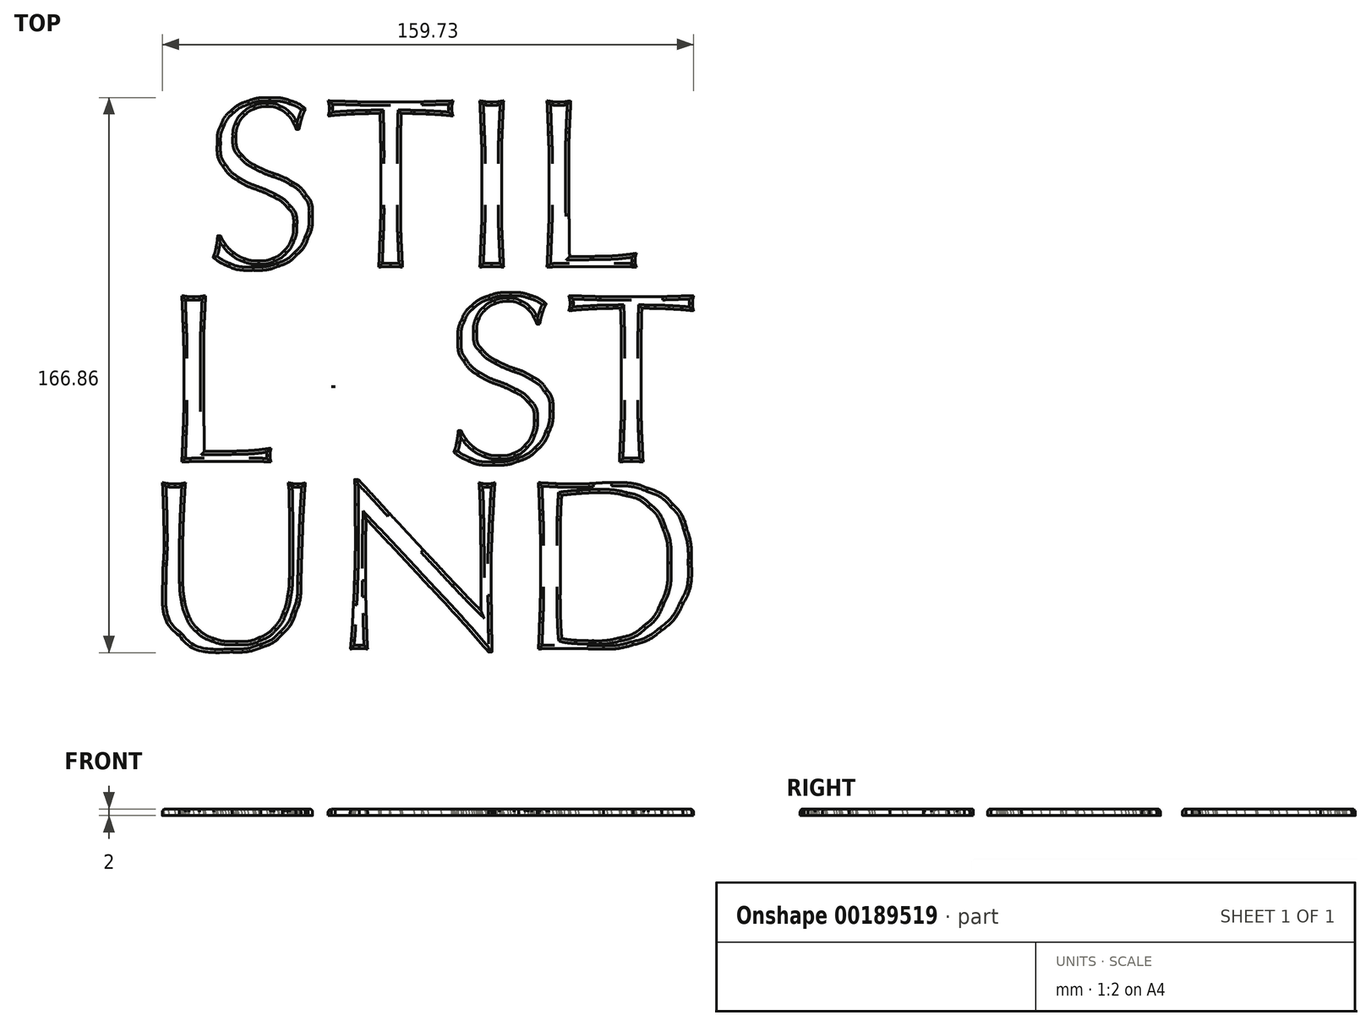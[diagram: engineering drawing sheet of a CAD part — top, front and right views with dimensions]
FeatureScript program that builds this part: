
annotation { "Feature Type Name" : "Feature", "Feature Type Description" : "" }
export const myFeature = defineFeature(function(context is Context, id is Id, definition is map)
    precondition{}
    {
        {
            var Q0;
            Q0=qCreatedBy(makeId("Top.planeOp"),FACE);
            var sketch = newSketch(context, id + "F0", { "sketchPlane" : qUnion([Q0])});
            skFitSpline(sketch, "E0", {"points": [v(-63.23, 41.86) * mm, v(-63.38, 40.46) * mm, v(-63.55, 39.3) * mm, v(-63.74, 38.37) * mm]});
            skFitSpline(sketch, "E1", {"points": [v(-63.74, 38.37) * mm, v(-63.9, 37.5) * mm, v(-64.18, 36.5) * mm, v(-64.62, 35.39) * mm]});
            skFitSpline(sketch, "E2", {"points": [v(-64.62, 35.39) * mm, v(-63.36, 34.37) * mm, v(-61.8, 33.44) * mm, v(-59.96, 32.62) * mm]});
            skFitSpline(sketch, "E3", {"points": [v(-59.96, 32.62) * mm, v(-58.07, 31.84) * mm, v(-55.62, 31.46) * mm, v(-52.6, 31.46) * mm]});
            skFitSpline(sketch, "E4", {"points": [v(-52.6, 31.46) * mm, v(-49.8, 31.46) * mm, v(-47.3, 31.84) * mm, v(-45.11, 32.62) * mm]});
            skFitSpline(sketch, "E5", {"points": [v(-45.11, 32.62) * mm, v(-42.88, 33.44) * mm, v(-41.01, 34.58) * mm, v(-39.5, 36.04) * mm]});
            skFitSpline(sketch, "E6", {"points": [v(-39.5, 36.04) * mm, v(-37.96, 37.54) * mm, v(-36.8, 39.3) * mm, v(-36.02, 41.28) * mm]});
            skFitSpline(sketch, "E7", {"points": [v(-36.02, 41.28) * mm, v(-35.2, 43.27) * mm, v(-34.78, 45.38) * mm, v(-34.78, 47.61) * mm]});
            skFitSpline(sketch, "E8", {"points": [v(-34.78, 47.61) * mm, v(-34.78, 50.28) * mm, v(-35.36, 52.42) * mm, v(-36.52, 54.02) * mm]});
            skFitSpline(sketch, "E9", {"points": [v(-36.52, 54.02) * mm, v(-37.64, 55.62) * mm, v(-39.05, 56.93) * mm, v(-40.75, 57.95) * mm]});
            skFitSpline(sketch, "E10", {"points": [v(-40.75, 57.95) * mm, v(-42.44, 58.97) * mm, v(-44.29, 59.82) * mm, v(-46.28, 60.5) * mm]});
            skFitSpline(sketch, "E11", {"points": [v(-46.28, 60.5) * mm, v(-48.22, 61.22) * mm, v(-50.04, 62.02) * mm, v(-51.74, 62.9) * mm]});
            skFitSpline(sketch, "E12", {"points": [v(-51.74, 62.9) * mm, v(-53.43, 63.82) * mm, v(-54.87, 64.93) * mm, v(-56.03, 66.24) * mm]});
            skFitSpline(sketch, "E13", {"points": [v(-56.03, 66.24) * mm, v(-57.15, 67.55) * mm, v(-57.7, 69.35) * mm, v(-57.7, 71.63) * mm]});
            skFitSpline(sketch, "E14", {"points": [v(-57.7, 71.63) * mm, v(-57.7, 72.94) * mm, v(-57.49, 74.15) * mm, v(-57.05, 75.27) * mm]});
            skFitSpline(sketch, "E15", {"points": [v(-57.05, 75.27) * mm, v(-56.56, 76.38) * mm, v(-55.9, 77.33) * mm, v(-55.08, 78.1) * mm]});
            skFitSpline(sketch, "E16", {"points": [v(-55.08, 78.1) * mm, v(-54.21, 78.93) * mm, v(-53.22, 79.56) * mm, v(-52.1, 80) * mm]});
            skFitSpline(sketch, "E17", {"points": [v(-52.1, 80) * mm, v(-50.94, 80.44) * mm, v(-49.67, 80.65) * mm, v(-48.32, 80.65) * mm]});
            skFitSpline(sketch, "E18", {"points": [v(-48.32, 80.65) * mm, v(-46.96, 80.65) * mm, v(-45.8, 80.41) * mm, v(-44.82, 79.93) * mm]});
            skFitSpline(sketch, "E19", {"points": [v(-44.82, 79.93) * mm, v(-43.85, 79.5) * mm, v(-43.03, 78.93) * mm, v(-42.35, 78.25) * mm]});
            skFitSpline(sketch, "E20", {"points": [v(-42.35, 78.25) * mm, v(-41.62, 77.57) * mm, v(-41.06, 76.82) * mm, v(-40.67, 76) * mm]});
            skFitSpline(sketch, "E21", {"points": [v(-40.67, 76) * mm, v(-40.24, 75.22) * mm, v(-39.9, 74.5) * mm, v(-39.65, 73.81) * mm]});
            skLineSegment(sketch, "E22", {"start": v(-62.36, 41.86) * mm, "end": v(-63.23, 41.86) * mm});
            skLineSegment(sketch, "E23", {"start": v(-63.23, 41.86) * mm, "end": v(-62.36, 41.86) * mm});
            skFitSpline(sketch, "E24", {"points": [v(-38.78, 73.81) * mm, v(-38.49, 75.22) * mm, v(-38.2, 76.38) * mm, v(-37.9, 77.3) * mm]});
            skFitSpline(sketch, "E25", {"points": [v(-37.9, 77.3) * mm, v(-37.62, 78.23) * mm, v(-37.25, 79.1) * mm, v(-36.82, 79.93) * mm]});
            skFitSpline(sketch, "E26", {"points": [v(-36.82, 79.93) * mm, v(-38.27, 81.1) * mm, v(-39.85, 81.94) * mm, v(-41.55, 82.47) * mm]});
            skFitSpline(sketch, "E27", {"points": [v(-41.55, 82.47) * mm, v(-43.24, 83.06) * mm, v(-45.26, 83.35) * mm, v(-47.59, 83.35) * mm]});
            skFitSpline(sketch, "E28", {"points": [v(-47.59, 83.35) * mm, v(-50.01, 83.35) * mm, v(-52.2, 83) * mm, v(-54.14, 82.33) * mm]});
            skFitSpline(sketch, "E29", {"points": [v(-54.14, 82.33) * mm, v(-56.08, 81.65) * mm, v(-57.75, 80.7) * mm, v(-59.16, 79.5) * mm]});
            skFitSpline(sketch, "E30", {"points": [v(-59.16, 79.5) * mm, v(-60.52, 78.28) * mm, v(-61.56, 76.82) * mm, v(-62.29, 75.12) * mm]});
            skFitSpline(sketch, "E31", {"points": [v(-62.29, 75.12) * mm, v(-63.02, 73.47) * mm, v(-63.38, 71.63) * mm, v(-63.38, 69.6) * mm]});
            skFitSpline(sketch, "E32", {"points": [v(-63.38, 69.6) * mm, v(-63.38, 66.73) * mm, v(-62.82, 64.45) * mm, v(-61.7, 62.75) * mm]});
            skFitSpline(sketch, "E33", {"points": [v(-61.7, 62.75) * mm, v(-60.54, 61.05) * mm, v(-59.11, 59.65) * mm, v(-57.41, 58.53) * mm]});
            skFitSpline(sketch, "E34", {"points": [v(-57.41, 58.53) * mm, v(-55.71, 57.46) * mm, v(-53.9, 56.56) * mm, v(-51.95, 55.84) * mm]});
            skFitSpline(sketch, "E35", {"points": [v(-51.95, 55.84) * mm, v(-49.96, 55.1) * mm, v(-48.12, 54.3) * mm, v(-46.42, 53.43) * mm]});
            skFitSpline(sketch, "E36", {"points": [v(-46.42, 53.43) * mm, v(-44.72, 52.56) * mm, v(-43.32, 51.47) * mm, v(-42.2, 50.16) * mm]});
            skFitSpline(sketch, "E37", {"points": [v(-42.2, 50.16) * mm, v(-41.04, 48.85) * mm, v(-40.45, 47.08) * mm, v(-40.45, 44.85) * mm]});
            skFitSpline(sketch, "E38", {"points": [v(-40.45, 44.85) * mm, v(-40.45, 43.4) * mm, v(-40.7, 42) * mm, v(-41.18, 40.7) * mm]});
            skFitSpline(sketch, "E39", {"points": [v(-41.18, 40.7) * mm, v(-41.67, 39.44) * mm, v(-42.37, 38.32) * mm, v(-43.3, 37.35) * mm]});
            skFitSpline(sketch, "E40", {"points": [v(-43.3, 37.35) * mm, v(-44.17, 36.43) * mm, v(-45.26, 35.68) * mm, v(-46.57, 35.1) * mm]});
            skFitSpline(sketch, "E41", {"points": [v(-46.57, 35.1) * mm, v(-47.83, 34.56) * mm, v(-49.26, 34.3) * mm, v(-50.86, 34.3) * mm]});
            skFitSpline(sketch, "E42", {"points": [v(-50.86, 34.3) * mm, v(-52.41, 34.3) * mm, v(-53.82, 34.51) * mm, v(-55.08, 34.95) * mm]});
            skFitSpline(sketch, "E43", {"points": [v(-55.08, 34.95) * mm, v(-56.35, 35.43) * mm, v(-57.46, 36.04) * mm, v(-58.43, 36.77) * mm]});
            skFitSpline(sketch, "E44", {"points": [v(-58.43, 36.77) * mm, v(-59.35, 37.5) * mm, v(-60.15, 38.3) * mm, v(-60.83, 39.17) * mm]});
            skFitSpline(sketch, "E45", {"points": [v(-60.83, 39.17) * mm, v(-61.46, 40.1) * mm, v(-61.97, 40.99) * mm, v(-62.36, 41.86) * mm]});
            skLineSegment(sketch, "E46", {"start": v(-39.65, 73.81) * mm, "end": v(-38.78, 73.81) * mm});
            skLineSegment(sketch, "E47", {"start": v(-38.78, 73.81) * mm, "end": v(-39.65, 73.81) * mm});
            skFitSpline(sketch, "E48", {"points": [v(-14.25, 51.03) * mm, v(-14.25, 47.83) * mm, v(-14.33, 44.68) * mm, v(-14.47, 41.57) * mm]});
            skFitSpline(sketch, "E49", {"points": [v(-14.47, 41.57) * mm, v(-14.57, 38.47) * mm, v(-14.7, 35.4) * mm, v(-14.84, 32.4) * mm]});
            skFitSpline(sketch, "E50", {"points": [v(-14.84, 32.4) * mm, v(-13.72, 32.5) * mm, v(-12.53, 32.55) * mm, v(-11.27, 32.55) * mm]});
            skFitSpline(sketch, "E51", {"points": [v(-11.27, 32.55) * mm, v(-10, 32.55) * mm, v(-8.82, 32.5) * mm, v(-7.7, 32.4) * mm]});
            skFitSpline(sketch, "E52", {"points": [v(-7.7, 32.4) * mm, v(-7.85, 35.4) * mm, v(-8, 38.47) * mm, v(-8.14, 41.57) * mm]});
            skFitSpline(sketch, "E53", {"points": [v(-8.14, 41.57) * mm, v(-8.24, 44.68) * mm, v(-8.29, 47.83) * mm, v(-8.29, 51.03) * mm]});
            skLineSegment(sketch, "E54", {"start": v(-14.25, 63.55) * mm, "end": v(-14.25, 51.03) * mm});
            skLineSegment(sketch, "E55", {"start": v(-14.25, 51.03) * mm, "end": v(-14.25, 63.55) * mm});
            skFitSpline(sketch, "E56", {"points": [v(-8.29, 63.55) * mm, v(-8.29, 68.6) * mm, v(-8.21, 73.62) * mm, v(-8.07, 78.62) * mm]});
            skFitSpline(sketch, "E57", {"points": [v(-8.07, 78.62) * mm, v(-6.8, 78.62) * mm, v(-5.5, 78.6) * mm, v(-4.14, 78.54) * mm]});
            skFitSpline(sketch, "E58", {"points": [v(-4.14, 78.54) * mm, v(-2.73, 78.54) * mm, v(-1.35, 78.5) * mm, v(0.01, 78.4) * mm]});
            skFitSpline(sketch, "E59", {"points": [v(0.01, 78.4) * mm, v(1.42, 78.35) * mm, v(2.75, 78.28) * mm, v(4.01, 78.18) * mm]});
            skFitSpline(sketch, "E60", {"points": [v(4.01, 78.18) * mm, v(5.32, 78.08) * mm, v(6.49, 77.96) * mm, v(7.5, 77.82) * mm]});
            skFitSpline(sketch, "E61", {"points": [v(7.5, 77.82) * mm, v(7.26, 78.69) * mm, v(7.14, 79.44) * mm, v(7.14, 80.07) * mm]});
            skFitSpline(sketch, "E62", {"points": [v(7.14, 80.07) * mm, v(7.14, 80.65) * mm, v(7.26, 81.43) * mm, v(7.5, 82.4) * mm]});
            skFitSpline(sketch, "E63", {"points": [v(7.5, 82.4) * mm, v(4.3, 82.3) * mm, v(1.18, 82.2) * mm, v(-1.88, 82.11) * mm]});
            skFitSpline(sketch, "E64", {"points": [v(-1.88, 82.11) * mm, v(-4.94, 82.06) * mm, v(-8.07, 82.04) * mm, v(-11.27, 82.04) * mm]});
            skFitSpline(sketch, "E65", {"points": [v(-11.27, 82.04) * mm, v(-14.47, 82.04) * mm, v(-17.6, 82.06) * mm, v(-20.66, 82.11) * mm]});
            skFitSpline(sketch, "E66", {"points": [v(-20.66, 82.11) * mm, v(-23.72, 82.2) * mm, v(-26.84, 82.3) * mm, v(-30.05, 82.4) * mm]});
            skFitSpline(sketch, "E67", {"points": [v(-30.05, 82.4) * mm, v(-29.8, 81.43) * mm, v(-29.68, 80.68) * mm, v(-29.68, 80.15) * mm]});
            skFitSpline(sketch, "E68", {"points": [v(-29.68, 80.15) * mm, v(-29.68, 79.47) * mm, v(-29.8, 78.69) * mm, v(-30.05, 77.82) * mm]});
            skFitSpline(sketch, "E69", {"points": [v(-30.05, 77.82) * mm, v(-29.03, 77.96) * mm, v(-27.89, 78.08) * mm, v(-26.63, 78.18) * mm]});
            skFitSpline(sketch, "E70", {"points": [v(-26.63, 78.18) * mm, v(-25.32, 78.28) * mm, v(-23.98, 78.35) * mm, v(-22.62, 78.4) * mm]});
            skFitSpline(sketch, "E71", {"points": [v(-22.62, 78.4) * mm, v(-21.22, 78.5) * mm, v(-19.83, 78.54) * mm, v(-18.48, 78.54) * mm]});
            skFitSpline(sketch, "E72", {"points": [v(-18.48, 78.54) * mm, v(-17.07, 78.6) * mm, v(-15.73, 78.62) * mm, v(-14.47, 78.62) * mm]});
            skFitSpline(sketch, "E73", {"points": [v(-14.47, 78.62) * mm, v(-14.33, 73.62) * mm, v(-14.25, 68.6) * mm, v(-14.25, 63.55) * mm]});
            skLineSegment(sketch, "E74", {"start": v(-8.29, 51.03) * mm, "end": v(-8.29, 63.55) * mm});
            skLineSegment(sketch, "E75", {"start": v(-8.29, 63.55) * mm, "end": v(-8.29, 51.03) * mm});
            skFitSpline(sketch, "E76", {"points": [v(16.14, 51.03) * mm, v(16.14, 47.83) * mm, v(16.07, 44.68) * mm, v(15.92, 41.57) * mm]});
            skFitSpline(sketch, "E77", {"points": [v(15.92, 41.57) * mm, v(15.83, 38.47) * mm, v(15.7, 35.4) * mm, v(15.56, 32.4) * mm]});
            skFitSpline(sketch, "E78", {"points": [v(15.56, 32.4) * mm, v(16.68, 32.5) * mm, v(17.86, 32.55) * mm, v(19.13, 32.55) * mm]});
            skFitSpline(sketch, "E79", {"points": [v(19.13, 32.55) * mm, v(20.39, 32.55) * mm, v(21.58, 32.5) * mm, v(22.7, 32.4) * mm]});
            skFitSpline(sketch, "E80", {"points": [v(22.7, 32.4) * mm, v(22.55, 35.4) * mm, v(22.4, 38.47) * mm, v(22.26, 41.57) * mm]});
            skFitSpline(sketch, "E81", {"points": [v(22.26, 41.57) * mm, v(22.16, 44.68) * mm, v(22.11, 47.83) * mm, v(22.11, 51.03) * mm]});
            skLineSegment(sketch, "E82", {"start": v(16.14, 63.55) * mm, "end": v(16.14, 51.03) * mm});
            skLineSegment(sketch, "E83", {"start": v(16.14, 51.03) * mm, "end": v(16.14, 63.55) * mm});
            skFitSpline(sketch, "E84", {"points": [v(22.11, 63.55) * mm, v(22.11, 66.75) * mm, v(22.16, 69.88) * mm, v(22.26, 72.94) * mm]});
            skFitSpline(sketch, "E85", {"points": [v(22.26, 72.94) * mm, v(22.4, 76.05) * mm, v(22.55, 79.2) * mm, v(22.7, 82.4) * mm]});
            skFitSpline(sketch, "E86", {"points": [v(22.7, 82.4) * mm, v(22.06, 82.3) * mm, v(21.46, 82.2) * mm, v(20.87, 82.11) * mm]});
            skFitSpline(sketch, "E87", {"points": [v(20.87, 82.11) * mm, v(20.3, 82.06) * mm, v(19.7, 82.04) * mm, v(19.13, 82.04) * mm]});
            skFitSpline(sketch, "E88", {"points": [v(19.13, 82.04) * mm, v(18.54, 82.04) * mm, v(17.96, 82.06) * mm, v(17.38, 82.11) * mm]});
            skFitSpline(sketch, "E89", {"points": [v(17.38, 82.11) * mm, v(16.8, 82.2) * mm, v(16.2, 82.3) * mm, v(15.56, 82.4) * mm]});
            skFitSpline(sketch, "E90", {"points": [v(15.56, 82.4) * mm, v(15.7, 79.2) * mm, v(15.83, 76.05) * mm, v(15.92, 72.94) * mm]});
            skFitSpline(sketch, "E91", {"points": [v(15.92, 72.94) * mm, v(16.07, 69.88) * mm, v(16.14, 66.75) * mm, v(16.14, 63.55) * mm]});
            skLineSegment(sketch, "E92", {"start": v(22.11, 51.03) * mm, "end": v(22.11, 63.55) * mm});
            skLineSegment(sketch, "E93", {"start": v(22.11, 63.55) * mm, "end": v(22.11, 51.03) * mm});
            skFitSpline(sketch, "E94", {"points": [v(36.33, 51.03) * mm, v(36.33, 47.83) * mm, v(36.25, 44.68) * mm, v(36.1, 41.57) * mm]});
            skFitSpline(sketch, "E95", {"points": [v(36.1, 41.57) * mm, v(36.01, 38.47) * mm, v(35.9, 35.4) * mm, v(35.74, 32.4) * mm]});
            skFitSpline(sketch, "E96", {"points": [v(35.74, 32.4) * mm, v(38.07, 32.5) * mm, v(40.3, 32.55) * mm, v(42.44, 32.55) * mm]});
            skFitSpline(sketch, "E97", {"points": [v(42.44, 32.55) * mm, v(44.62, 32.55) * mm, v(46.88, 32.55) * mm, v(49.2, 32.55) * mm]});
            skFitSpline(sketch, "E98", {"points": [v(49.2, 32.55) * mm, v(51.44, 32.55) * mm, v(53.67, 32.55) * mm, v(55.9, 32.55) * mm]});
            skFitSpline(sketch, "E99", {"points": [v(55.9, 32.55) * mm, v(58.14, 32.55) * mm, v(60.37, 32.5) * mm, v(62.6, 32.4) * mm]});
            skFitSpline(sketch, "E100", {"points": [v(62.6, 32.4) * mm, v(62.36, 33.18) * mm, v(62.24, 33.83) * mm, v(62.24, 34.37) * mm]});
            skFitSpline(sketch, "E101", {"points": [v(62.24, 34.37) * mm, v(62.24, 34.95) * mm, v(62.36, 35.68) * mm, v(62.6, 36.55) * mm]});
            skFitSpline(sketch, "E102", {"points": [v(62.6, 36.55) * mm, v(58.96, 36.06) * mm, v(55.57, 35.77) * mm, v(52.41, 35.68) * mm]});
            skFitSpline(sketch, "E103", {"points": [v(52.41, 35.68) * mm, v(49.26, 35.63) * mm, v(45.96, 35.6) * mm, v(42.51, 35.6) * mm]});
            skFitSpline(sketch, "E104", {"points": [v(42.51, 35.6) * mm, v(42.46, 39.15) * mm, v(42.42, 43.15) * mm, v(42.37, 47.61) * mm]});
            skFitSpline(sketch, "E105", {"points": [v(42.37, 47.61) * mm, v(42.32, 52.12) * mm, v(42.3, 57.44) * mm, v(42.3, 63.55) * mm]});
            skFitSpline(sketch, "E106", {"points": [v(42.3, 63.55) * mm, v(42.3, 66.75) * mm, v(42.34, 69.88) * mm, v(42.44, 72.94) * mm]});
            skFitSpline(sketch, "E107", {"points": [v(42.44, 72.94) * mm, v(42.59, 76.05) * mm, v(42.73, 79.2) * mm, v(42.88, 82.4) * mm]});
            skFitSpline(sketch, "E108", {"points": [v(42.88, 82.4) * mm, v(42.25, 82.3) * mm, v(41.64, 82.2) * mm, v(41.06, 82.11) * mm]});
            skFitSpline(sketch, "E109", {"points": [v(41.06, 82.11) * mm, v(40.48, 82.06) * mm, v(39.9, 82.04) * mm, v(39.31, 82.04) * mm]});
            skFitSpline(sketch, "E110", {"points": [v(39.31, 82.04) * mm, v(38.73, 82.04) * mm, v(38.15, 82.06) * mm, v(37.56, 82.11) * mm]});
            skFitSpline(sketch, "E111", {"points": [v(37.56, 82.11) * mm, v(36.98, 82.2) * mm, v(36.38, 82.3) * mm, v(35.74, 82.4) * mm]});
            skFitSpline(sketch, "E112", {"points": [v(35.74, 82.4) * mm, v(35.9, 79.2) * mm, v(36.01, 76.05) * mm, v(36.1, 72.94) * mm]});
            skFitSpline(sketch, "E113", {"points": [v(36.1, 72.94) * mm, v(36.25, 69.88) * mm, v(36.33, 66.75) * mm, v(36.33, 63.55) * mm]});
            skLineSegment(sketch, "E114", {"start": v(36.33, 63.55) * mm, "end": v(36.33, 51.03) * mm});
            skLineSegment(sketch, "E115", {"start": v(36.33, 51.03) * mm, "end": v(36.33, 63.55) * mm});
            skFitSpline(sketch, "E116", {"points": [v(-73.44, -7.54) * mm, v(-73.44, -10.74) * mm, v(-73.51, -13.9) * mm, v(-73.66, -17) * mm]});
            skFitSpline(sketch, "E117", {"points": [v(-73.66, -17) * mm, v(-73.75, -20.1) * mm, v(-73.88, -23.17) * mm, v(-74.02, -26.17) * mm]});
            skFitSpline(sketch, "E118", {"points": [v(-74.02, -26.17) * mm, v(-71.7, -26.08) * mm, v(-69.46, -26.03) * mm, v(-67.33, -26.03) * mm]});
            skFitSpline(sketch, "E119", {"points": [v(-67.33, -26.03) * mm, v(-65.14, -26.03) * mm, v(-62.89, -26.03) * mm, v(-60.56, -26.03) * mm]});
            skFitSpline(sketch, "E120", {"points": [v(-60.56, -26.03) * mm, v(-58.32, -26.03) * mm, v(-56.1, -26.03) * mm, v(-53.86, -26.03) * mm]});
            skFitSpline(sketch, "E121", {"points": [v(-53.86, -26.03) * mm, v(-51.63, -26.03) * mm, v(-49.4, -26.08) * mm, v(-47.17, -26.17) * mm]});
            skFitSpline(sketch, "E122", {"points": [v(-47.17, -26.17) * mm, v(-47.4, -25.4) * mm, v(-47.53, -24.74) * mm, v(-47.53, -24.2) * mm]});
            skFitSpline(sketch, "E123", {"points": [v(-47.53, -24.2) * mm, v(-47.53, -23.63) * mm, v(-47.4, -22.9) * mm, v(-47.17, -22.03) * mm]});
            skFitSpline(sketch, "E124", {"points": [v(-47.17, -22.03) * mm, v(-50.8, -22.51) * mm, v(-54.2, -22.8) * mm, v(-57.35, -22.9) * mm]});
            skFitSpline(sketch, "E125", {"points": [v(-57.35, -22.9) * mm, v(-60.5, -22.95) * mm, v(-63.8, -22.97) * mm, v(-67.25, -22.97) * mm]});
            skFitSpline(sketch, "E126", {"points": [v(-67.25, -22.97) * mm, v(-67.3, -19.43) * mm, v(-67.35, -15.43) * mm, v(-67.4, -10.96) * mm]});
            skFitSpline(sketch, "E127", {"points": [v(-67.4, -10.96) * mm, v(-67.45, -6.45) * mm, v(-67.47, -1.14) * mm, v(-67.47, 4.98) * mm]});
            skFitSpline(sketch, "E128", {"points": [v(-67.47, 4.98) * mm, v(-67.47, 8.18) * mm, v(-67.42, 11.3) * mm, v(-67.33, 14.36) * mm]});
            skFitSpline(sketch, "E129", {"points": [v(-67.33, 14.36) * mm, v(-67.18, 17.47) * mm, v(-67.03, 20.62) * mm, v(-66.89, 23.83) * mm]});
            skFitSpline(sketch, "E130", {"points": [v(-66.89, 23.83) * mm, v(-67.52, 23.73) * mm, v(-68.13, 23.63) * mm, v(-68.7, 23.53) * mm]});
            skFitSpline(sketch, "E131", {"points": [v(-68.7, 23.53) * mm, v(-69.3, 23.49) * mm, v(-69.87, 23.46) * mm, v(-70.45, 23.46) * mm]});
            skFitSpline(sketch, "E132", {"points": [v(-70.45, 23.46) * mm, v(-71.04, 23.46) * mm, v(-71.62, 23.49) * mm, v(-72.2, 23.53) * mm]});
            skFitSpline(sketch, "E133", {"points": [v(-72.2, 23.53) * mm, v(-72.78, 23.63) * mm, v(-73.4, 23.73) * mm, v(-74.02, 23.83) * mm]});
            skFitSpline(sketch, "E134", {"points": [v(-74.02, 23.83) * mm, v(-73.88, 20.62) * mm, v(-73.75, 17.47) * mm, v(-73.66, 14.36) * mm]});
            skFitSpline(sketch, "E135", {"points": [v(-73.66, 14.36) * mm, v(-73.51, 11.3) * mm, v(-73.44, 8.18) * mm, v(-73.44, 4.98) * mm]});
            skLineSegment(sketch, "E136", {"start": v(-73.44, 4.98) * mm, "end": v(-73.44, -7.54) * mm});
            skLineSegment(sketch, "E137", {"start": v(-73.44, -7.54) * mm, "end": v(-73.44, 4.98) * mm});
            skFitSpline(sketch, "E138", {"points": [v(-29.12, -3.54) * mm, v(-27.85, -3.54) * mm, v(-26.54, -3.56) * mm, v(-25.19, -3.61) * mm]});
            skFitSpline(sketch, "E139", {"points": [v(-25.19, -3.61) * mm, v(-23.83, -3.66) * mm, v(-22.52, -3.68) * mm, v(-21.26, -3.68) * mm]});
            skFitSpline(sketch, "E140", {"points": [v(-21.26, -3.68) * mm, v(-19.9, -3.68) * mm, v(-18.54, -3.68) * mm, v(-17.18, -3.68) * mm]});
            skFitSpline(sketch, "E141", {"points": [v(-17.18, -3.68) * mm, v(-15.82, -3.64) * mm, v(-14.46, -3.59) * mm, v(-13.1, -3.54) * mm]});
            skFitSpline(sketch, "E142", {"points": [v(3.13, -26.17) * mm, v(2.45, -26.08) * mm, v(1.8, -26.03) * mm, v(1.16, -26.03) * mm]});
            skFitSpline(sketch, "E143", {"points": [v(1.16, -26.03) * mm, v(0.58, -26.03) * mm, v(-0.05, -26.03) * mm, v(-0.73, -26.03) * mm]});
            skFitSpline(sketch, "E144", {"points": [v(-0.73, -26.03) * mm, v(-1.41, -26.03) * mm, v(-2.07, -26.03) * mm, v(-2.7, -26.03) * mm]});
            skFitSpline(sketch, "E145", {"points": [v(-2.7, -26.03) * mm, v(-3.28, -26.03) * mm, v(-3.9, -26.08) * mm, v(-4.59, -26.17) * mm]});
            skFitSpline(sketch, "E146", {"points": [v(-4.59, -26.17) * mm, v(-4.93, -25.06) * mm, v(-5.39, -23.72) * mm, v(-5.97, -22.17) * mm]});
            skFitSpline(sketch, "E147", {"points": [v(-5.97, -22.17) * mm, v(-6.55, -20.57) * mm, v(-7.2, -18.92) * mm, v(-7.94, -17.22) * mm]});
            skFitSpline(sketch, "E148", {"points": [v(-7.94, -17.22) * mm, v(-8.62, -15.48) * mm, v(-9.32, -13.73) * mm, v(-10.05, -11.98) * mm]});
            skFitSpline(sketch, "E149", {"points": [v(-10.05, -11.98) * mm, v(-10.77, -10.19) * mm, v(-11.45, -8.49) * mm, v(-12.08, -6.89) * mm]});
            skFitSpline(sketch, "E150", {"points": [v(-12.08, -6.89) * mm, v(-13.64, -6.84) * mm, v(-15.21, -6.81) * mm, v(-16.82, -6.81) * mm]});
            skFitSpline(sketch, "E151", {"points": [v(-16.82, -6.81) * mm, v(-18.42, -6.77) * mm, v(-20.02, -6.74) * mm, v(-21.62, -6.74) * mm]});
            skFitSpline(sketch, "E152", {"points": [v(-21.62, -6.74) * mm, v(-23.12, -6.74) * mm, v(-24.6, -6.77) * mm, v(-26.06, -6.81) * mm]});
            skFitSpline(sketch, "E153", {"points": [v(-26.06, -6.81) * mm, v(-27.51, -6.81) * mm, v(-29, -6.84) * mm, v(-30.5, -6.89) * mm]});
            skFitSpline(sketch, "E154", {"points": [v(-30.5, -6.89) * mm, v(-32.05, -10.67) * mm, v(-33.46, -14.29) * mm, v(-34.72, -17.73) * mm]});
            skFitSpline(sketch, "E155", {"points": [v(-34.72, -17.73) * mm, v(-35.98, -21.13) * mm, v(-36.93, -23.94) * mm, v(-37.56, -26.17) * mm]});
            skFitSpline(sketch, "E156", {"points": [v(-37.56, -26.17) * mm, v(-38.38, -26.08) * mm, v(-39.28, -26.03) * mm, v(-40.25, -26.03) * mm]});
            skFitSpline(sketch, "E157", {"points": [v(-40.25, -26.03) * mm, v(-41.22, -26.03) * mm, v(-42.12, -26.08) * mm, v(-42.94, -26.17) * mm]});
            skFitSpline(sketch, "E158", {"points": [v(-42.94, -26.17) * mm, v(-39.01, -17.68) * mm, v(-35.18, -9.24) * mm, v(-31.44, -0.85) * mm]});
            skFitSpline(sketch, "E159", {"points": [v(-31.44, -0.85) * mm, v(-27.7, 7.55) * mm, v(-23.95, 16.09) * mm, v(-20.16, 24.77) * mm]});
            skLineSegment(sketch, "E160", {"start": v(-13.1, -3.54) * mm, "end": v(-21.18, 14.95) * mm});
            skLineSegment(sketch, "E161", {"start": v(-21.18, 14.95) * mm, "end": v(-29.12, -3.54) * mm});
            skLineSegment(sketch, "E162", {"start": v(-29.12, -3.54) * mm, "end": v(-13.1, -3.54) * mm});
            skFitSpline(sketch, "E163", {"points": [v(-18.78, 24.77) * mm, v(-17.62, 21.96) * mm, v(-16.35, 18.9) * mm, v(-15, 15.6) * mm]});
            skFitSpline(sketch, "E164", {"points": [v(-15, 15.6) * mm, v(-13.64, 12.35) * mm, v(-12.25, 9.05) * mm, v(-10.85, 5.7) * mm]});
            skFitSpline(sketch, "E165", {"points": [v(-10.85, 5.7) * mm, v(-9.44, 2.36) * mm, v(-8.03, -0.97) * mm, v(-6.63, -4.27) * mm]});
            skFitSpline(sketch, "E166", {"points": [v(-6.63, -4.27) * mm, v(-5.22, -7.57) * mm, v(-3.9, -10.65) * mm, v(-2.7, -13.51) * mm]});
            skFitSpline(sketch, "E167", {"points": [v(-2.7, -13.51) * mm, v(-1.43, -16.32) * mm, v(-0.32, -18.85) * mm, v(0.65, -21.08) * mm]});
            skFitSpline(sketch, "E168", {"points": [v(0.65, -21.08) * mm, v(1.67, -23.31) * mm, v(2.5, -25) * mm, v(3.13, -26.17) * mm]});
            skLineSegment(sketch, "E169", {"start": v(-20.16, 24.77) * mm, "end": v(-18.78, 24.77) * mm});
            skLineSegment(sketch, "E170", {"start": v(-18.78, 24.77) * mm, "end": v(-20.16, 24.77) * mm});
            skFitSpline(sketch, "E171", {"points": [v(9.1, -16.71) * mm, v(8.95, -18.12) * mm, v(8.78, -19.28) * mm, v(8.58, -20.2) * mm]});
            skFitSpline(sketch, "E172", {"points": [v(8.58, -20.2) * mm, v(8.44, -21.08) * mm, v(8.15, -22.07) * mm, v(7.7, -23.19) * mm]});
            skFitSpline(sketch, "E173", {"points": [v(7.7, -23.19) * mm, v(8.97, -24.2) * mm, v(10.52, -25.13) * mm, v(12.37, -25.96) * mm]});
            skFitSpline(sketch, "E174", {"points": [v(12.37, -25.96) * mm, v(14.26, -26.73) * mm, v(16.7, -27.12) * mm, v(19.72, -27.12) * mm]});
            skFitSpline(sketch, "E175", {"points": [v(19.72, -27.12) * mm, v(22.53, -27.12) * mm, v(25.03, -26.73) * mm, v(27.21, -25.96) * mm]});
            skFitSpline(sketch, "E176", {"points": [v(27.21, -25.96) * mm, v(29.45, -25.13) * mm, v(31.31, -24) * mm, v(32.82, -22.53) * mm]});
            skFitSpline(sketch, "E177", {"points": [v(32.82, -22.53) * mm, v(34.37, -21.03) * mm, v(35.54, -19.28) * mm, v(36.31, -17.3) * mm]});
            skFitSpline(sketch, "E178", {"points": [v(36.31, -17.3) * mm, v(37.14, -15.3) * mm, v(37.55, -13.2) * mm, v(37.55, -10.96) * mm]});
            skFitSpline(sketch, "E179", {"points": [v(37.55, -10.96) * mm, v(37.55, -8.3) * mm, v(36.97, -6.16) * mm, v(35.8, -4.56) * mm]});
            skFitSpline(sketch, "E180", {"points": [v(35.8, -4.56) * mm, v(34.69, -2.96) * mm, v(33.28, -1.65) * mm, v(31.58, -0.63) * mm]});
            skFitSpline(sketch, "E181", {"points": [v(31.58, -0.63) * mm, v(29.88, 0.4) * mm, v(28.04, 1.24) * mm, v(26.05, 1.92) * mm]});
            skFitSpline(sketch, "E182", {"points": [v(26.05, 1.92) * mm, v(24.1, 2.65) * mm, v(22.29, 3.45) * mm, v(20.6, 4.32) * mm]});
            skFitSpline(sketch, "E183", {"points": [v(20.6, 4.32) * mm, v(18.9, 5.24) * mm, v(17.46, 6.36) * mm, v(16.3, 7.67) * mm]});
            skFitSpline(sketch, "E184", {"points": [v(16.3, 7.67) * mm, v(15.18, 8.98) * mm, v(14.62, 10.77) * mm, v(14.62, 13.05) * mm]});
            skFitSpline(sketch, "E185", {"points": [v(14.62, 13.05) * mm, v(14.62, 14.36) * mm, v(14.84, 15.58) * mm, v(15.28, 16.7) * mm]});
            skFitSpline(sketch, "E186", {"points": [v(15.28, 16.7) * mm, v(15.76, 17.8) * mm, v(16.42, 18.76) * mm, v(17.24, 19.53) * mm]});
            skFitSpline(sketch, "E187", {"points": [v(17.24, 19.53) * mm, v(18.12, 20.36) * mm, v(19.11, 20.99) * mm, v(20.23, 21.42) * mm]});
            skFitSpline(sketch, "E188", {"points": [v(20.23, 21.42) * mm, v(21.4, 21.86) * mm, v(22.65, 22.08) * mm, v(24.01, 22.08) * mm]});
            skFitSpline(sketch, "E189", {"points": [v(24.01, 22.08) * mm, v(25.37, 22.08) * mm, v(26.53, 21.84) * mm, v(27.5, 21.35) * mm]});
            skFitSpline(sketch, "E190", {"points": [v(27.5, 21.35) * mm, v(28.48, 20.91) * mm, v(29.3, 20.36) * mm, v(29.98, 19.68) * mm]});
            skFitSpline(sketch, "E191", {"points": [v(29.98, 19.68) * mm, v(30.7, 19) * mm, v(31.27, 18.25) * mm, v(31.65, 17.42) * mm]});
            skFitSpline(sketch, "E192", {"points": [v(31.65, 17.42) * mm, v(32.1, 16.65) * mm, v(32.43, 15.92) * mm, v(32.67, 15.24) * mm]});
            skLineSegment(sketch, "E193", {"start": v(9.97, -16.71) * mm, "end": v(9.1, -16.71) * mm});
            skLineSegment(sketch, "E194", {"start": v(9.1, -16.71) * mm, "end": v(9.97, -16.71) * mm});
            skFitSpline(sketch, "E195", {"points": [v(33.55, 15.24) * mm, v(33.84, 16.65) * mm, v(34.13, 17.8) * mm, v(34.42, 18.73) * mm]});
            skFitSpline(sketch, "E196", {"points": [v(34.42, 18.73) * mm, v(34.71, 19.65) * mm, v(35.07, 20.53) * mm, v(35.51, 21.35) * mm]});
            skFitSpline(sketch, "E197", {"points": [v(35.51, 21.35) * mm, v(34.06, 22.52) * mm, v(32.48, 23.37) * mm, v(30.78, 23.9) * mm]});
            skFitSpline(sketch, "E198", {"points": [v(30.78, 23.9) * mm, v(29.08, 24.48) * mm, v(27.07, 24.77) * mm, v(24.74, 24.77) * mm]});
            skFitSpline(sketch, "E199", {"points": [v(24.74, 24.77) * mm, v(22.31, 24.77) * mm, v(20.13, 24.43) * mm, v(18.19, 23.75) * mm]});
            skFitSpline(sketch, "E200", {"points": [v(18.19, 23.75) * mm, v(16.25, 23.07) * mm, v(14.57, 22.13) * mm, v(13.17, 20.91) * mm]});
            skFitSpline(sketch, "E201", {"points": [v(13.17, 20.91) * mm, v(11.8, 19.7) * mm, v(10.77, 18.25) * mm, v(10.04, 16.55) * mm]});
            skFitSpline(sketch, "E202", {"points": [v(10.04, 16.55) * mm, v(9.31, 14.9) * mm, v(8.95, 13.05) * mm, v(8.95, 11.02) * mm]});
            skFitSpline(sketch, "E203", {"points": [v(8.95, 11.02) * mm, v(8.95, 8.15) * mm, v(9.5, 5.87) * mm, v(10.62, 4.18) * mm]});
            skFitSpline(sketch, "E204", {"points": [v(10.62, 4.18) * mm, v(11.78, 2.48) * mm, v(13.22, 1.07) * mm, v(14.91, -0.05) * mm]});
            skFitSpline(sketch, "E205", {"points": [v(14.91, -0.05) * mm, v(16.61, -1.11) * mm, v(18.43, -2.01) * mm, v(20.37, -2.74) * mm]});
            skFitSpline(sketch, "E206", {"points": [v(20.37, -2.74) * mm, v(22.36, -3.47) * mm, v(24.2, -4.27) * mm, v(25.9, -5.14) * mm]});
            skFitSpline(sketch, "E207", {"points": [v(25.9, -5.14) * mm, v(27.6, -6.01) * mm, v(29, -7.1) * mm, v(30.13, -8.42) * mm]});
            skFitSpline(sketch, "E208", {"points": [v(30.13, -8.42) * mm, v(31.29, -9.73) * mm, v(31.87, -11.5) * mm, v(31.87, -13.73) * mm]});
            skFitSpline(sketch, "E209", {"points": [v(31.87, -13.73) * mm, v(31.87, -15.18) * mm, v(31.63, -16.57) * mm, v(31.14, -17.88) * mm]});
            skFitSpline(sketch, "E210", {"points": [v(31.14, -17.88) * mm, v(30.66, -19.14) * mm, v(29.96, -20.25) * mm, v(29.03, -21.22) * mm]});
            skFitSpline(sketch, "E211", {"points": [v(29.03, -21.22) * mm, v(28.16, -22.15) * mm, v(27.07, -22.9) * mm, v(25.76, -23.48) * mm]});
            skFitSpline(sketch, "E212", {"points": [v(25.76, -23.48) * mm, v(24.5, -24.01) * mm, v(23.07, -24.28) * mm, v(21.46, -24.28) * mm]});
            skFitSpline(sketch, "E213", {"points": [v(21.46, -24.28) * mm, v(19.91, -24.28) * mm, v(18.5, -24.06) * mm, v(17.24, -23.63) * mm]});
            skFitSpline(sketch, "E214", {"points": [v(17.24, -23.63) * mm, v(15.98, -23.14) * mm, v(14.87, -22.53) * mm, v(13.9, -21.8) * mm]});
            skFitSpline(sketch, "E215", {"points": [v(13.9, -21.8) * mm, v(12.97, -21.08) * mm, v(12.17, -20.28) * mm, v(11.5, -19.4) * mm]});
            skFitSpline(sketch, "E216", {"points": [v(11.5, -19.4) * mm, v(10.86, -18.48) * mm, v(10.35, -17.59) * mm, v(9.97, -16.71) * mm]});
            skLineSegment(sketch, "E217", {"start": v(32.67, 15.24) * mm, "end": v(33.55, 15.24) * mm});
            skLineSegment(sketch, "E218", {"start": v(33.55, 15.24) * mm, "end": v(32.67, 15.24) * mm});
            skFitSpline(sketch, "E219", {"points": [v(58.07, -7.54) * mm, v(58.07, -10.74) * mm, v(58, -13.9) * mm, v(57.85, -17) * mm]});
            skFitSpline(sketch, "E220", {"points": [v(57.85, -17) * mm, v(57.76, -20.1) * mm, v(57.64, -23.17) * mm, v(57.5, -26.17) * mm]});
            skFitSpline(sketch, "E221", {"points": [v(57.5, -26.17) * mm, v(58.6, -26.08) * mm, v(59.8, -26.03) * mm, v(61.06, -26.03) * mm]});
            skFitSpline(sketch, "E222", {"points": [v(61.06, -26.03) * mm, v(62.32, -26.03) * mm, v(63.5, -26.08) * mm, v(64.62, -26.17) * mm]});
            skFitSpline(sketch, "E223", {"points": [v(64.62, -26.17) * mm, v(64.48, -23.17) * mm, v(64.33, -20.1) * mm, v(64.19, -17) * mm]});
            skFitSpline(sketch, "E224", {"points": [v(64.19, -17) * mm, v(64.09, -13.9) * mm, v(64.04, -10.74) * mm, v(64.04, -7.54) * mm]});
            skLineSegment(sketch, "E225", {"start": v(58.07, 4.98) * mm, "end": v(58.07, -7.54) * mm});
            skLineSegment(sketch, "E226", {"start": v(58.07, -7.54) * mm, "end": v(58.07, 4.98) * mm});
            skFitSpline(sketch, "E227", {"points": [v(64.04, 4.98) * mm, v(64.04, 10.02) * mm, v(64.11, 15.04) * mm, v(64.26, 20.04) * mm]});
            skFitSpline(sketch, "E228", {"points": [v(64.26, 20.04) * mm, v(65.52, 20.04) * mm, v(66.83, 20.02) * mm, v(68.19, 19.97) * mm]});
            skFitSpline(sketch, "E229", {"points": [v(68.19, 19.97) * mm, v(69.6, 19.97) * mm, v(70.98, 19.92) * mm, v(72.34, 19.82) * mm]});
            skFitSpline(sketch, "E230", {"points": [v(72.34, 19.82) * mm, v(73.74, 19.77) * mm, v(75.08, 19.7) * mm, v(76.34, 19.6) * mm]});
            skFitSpline(sketch, "E231", {"points": [v(76.34, 19.6) * mm, v(77.65, 19.5) * mm, v(78.82, 19.39) * mm, v(79.83, 19.24) * mm]});
            skFitSpline(sketch, "E232", {"points": [v(79.83, 19.24) * mm, v(79.6, 20.11) * mm, v(79.47, 20.87) * mm, v(79.47, 21.5) * mm]});
            skFitSpline(sketch, "E233", {"points": [v(79.47, 21.5) * mm, v(79.47, 22.08) * mm, v(79.6, 22.86) * mm, v(79.83, 23.83) * mm]});
            skFitSpline(sketch, "E234", {"points": [v(79.83, 23.83) * mm, v(76.63, 23.73) * mm, v(73.5, 23.63) * mm, v(70.45, 23.53) * mm]});
            skFitSpline(sketch, "E235", {"points": [v(70.45, 23.53) * mm, v(67.39, 23.49) * mm, v(64.26, 23.46) * mm, v(61.06, 23.46) * mm]});
            skFitSpline(sketch, "E236", {"points": [v(61.06, 23.46) * mm, v(57.85, 23.46) * mm, v(54.72, 23.49) * mm, v(51.67, 23.53) * mm]});
            skFitSpline(sketch, "E237", {"points": [v(51.67, 23.53) * mm, v(48.61, 23.63) * mm, v(45.48, 23.73) * mm, v(42.28, 23.83) * mm]});
            skFitSpline(sketch, "E238", {"points": [v(42.28, 23.83) * mm, v(42.52, 22.86) * mm, v(42.64, 22.1) * mm, v(42.64, 21.57) * mm]});
            skFitSpline(sketch, "E239", {"points": [v(42.64, 21.57) * mm, v(42.64, 20.9) * mm, v(42.52, 20.11) * mm, v(42.28, 19.24) * mm]});
            skFitSpline(sketch, "E240", {"points": [v(42.28, 19.24) * mm, v(43.3, 19.39) * mm, v(44.44, 19.5) * mm, v(45.7, 19.6) * mm]});
            skFitSpline(sketch, "E241", {"points": [v(45.7, 19.6) * mm, v(47.01, 19.7) * mm, v(48.34, 19.77) * mm, v(49.7, 19.82) * mm]});
            skFitSpline(sketch, "E242", {"points": [v(49.7, 19.82) * mm, v(51.11, 19.92) * mm, v(52.5, 19.97) * mm, v(53.85, 19.97) * mm]});
            skFitSpline(sketch, "E243", {"points": [v(53.85, 19.97) * mm, v(55.26, 20.02) * mm, v(56.6, 20.04) * mm, v(57.85, 20.04) * mm]});
            skFitSpline(sketch, "E244", {"points": [v(57.85, 20.04) * mm, v(58, 15.04) * mm, v(58.07, 10.02) * mm, v(58.07, 4.98) * mm]});
            skLineSegment(sketch, "E245", {"start": v(64.04, -7.54) * mm, "end": v(64.04, 4.98) * mm});
            skLineSegment(sketch, "E246", {"start": v(64.04, 4.98) * mm, "end": v(64.04, -7.54) * mm});
            skFitSpline(sketch, "E247", {"points": [v(-41.62, -56.06) * mm, v(-41.62, -57.56) * mm, v(-41.65, -59.2) * mm, v(-41.7, -61) * mm]});
            skFitSpline(sketch, "E248", {"points": [v(-41.7, -61) * mm, v(-41.75, -62.8) * mm, v(-41.92, -64.6) * mm, v(-42.2, -66.39) * mm]});
            skFitSpline(sketch, "E249", {"points": [v(-42.2, -66.39) * mm, v(-42.5, -68.19) * mm, v(-42.98, -69.9) * mm, v(-43.66, -71.56) * mm]});
            skFitSpline(sketch, "E250", {"points": [v(-43.66, -71.56) * mm, v(-44.3, -73.2) * mm, v(-45.2, -74.66) * mm, v(-46.36, -75.92) * mm]});
            skFitSpline(sketch, "E251", {"points": [v(-46.36, -75.92) * mm, v(-47.52, -77.19) * mm, v(-49.02, -78.2) * mm, v(-50.87, -78.98) * mm]});
            skFitSpline(sketch, "E252", {"points": [v(-50.87, -78.98) * mm, v(-52.66, -79.76) * mm, v(-54.9, -80.15) * mm, v(-57.56, -80.15) * mm]});
            skFitSpline(sketch, "E253", {"points": [v(-57.56, -80.15) * mm, v(-60.28, -80.15) * mm, v(-62.56, -79.83) * mm, v(-64.4, -79.2) * mm]});
            skFitSpline(sketch, "E254", {"points": [v(-64.4, -79.2) * mm, v(-66.25, -78.52) * mm, v(-67.78, -77.62) * mm, v(-68.99, -76.5) * mm]});
            skFitSpline(sketch, "E255", {"points": [v(-68.99, -76.5) * mm, v(-70.2, -75.34) * mm, v(-71.15, -74) * mm, v(-71.83, -72.5) * mm]});
            skFitSpline(sketch, "E256", {"points": [v(-71.83, -72.5) * mm, v(-72.46, -70.95) * mm, v(-72.92, -69.35) * mm, v(-73.21, -67.7) * mm]});
            skFitSpline(sketch, "E257", {"points": [v(-73.21, -67.7) * mm, v(-73.5, -66) * mm, v(-73.67, -64.28) * mm, v(-73.72, -62.53) * mm]});
            skFitSpline(sketch, "E258", {"points": [v(-73.72, -62.53) * mm, v(-73.77, -60.74) * mm, v(-73.8, -59.01) * mm, v(-73.8, -57.37) * mm]});
            skFitSpline(sketch, "E259", {"points": [v(-73.8, -57.37) * mm, v(-73.8, -54.65) * mm, v(-73.77, -52.03) * mm, v(-73.72, -49.5) * mm]});
            skFitSpline(sketch, "E260", {"points": [v(-73.72, -49.5) * mm, v(-73.67, -46.98) * mm, v(-73.6, -44.63) * mm, v(-73.5, -42.45) * mm]});
            skFitSpline(sketch, "E261", {"points": [v(-73.5, -42.45) * mm, v(-73.4, -40.26) * mm, v(-73.3, -38.32) * mm, v(-73.21, -36.62) * mm]});
            skFitSpline(sketch, "E262", {"points": [v(-73.21, -36.62) * mm, v(-73.11, -34.88) * mm, v(-73.02, -33.47) * mm, v(-72.92, -32.4) * mm]});
            skFitSpline(sketch, "E263", {"points": [v(-72.92, -32.4) * mm, v(-73.45, -32.5) * mm, v(-73.99, -32.6) * mm, v(-74.52, -32.7) * mm]});
            skFitSpline(sketch, "E264", {"points": [v(-74.52, -32.7) * mm, v(-75, -32.74) * mm, v(-75.52, -32.77) * mm, v(-76.05, -32.77) * mm]});
            skFitSpline(sketch, "E265", {"points": [v(-76.05, -32.77) * mm, v(-76.63, -32.77) * mm, v(-77.26, -32.74) * mm, v(-77.94, -32.7) * mm]});
            skFitSpline(sketch, "E266", {"points": [v(-77.94, -32.7) * mm, v(-78.62, -32.6) * mm, v(-79.25, -32.5) * mm, v(-79.83, -32.4) * mm]});
            skFitSpline(sketch, "E267", {"points": [v(-79.83, -32.4) * mm, v(-79.74, -34.58) * mm, v(-79.64, -37.25) * mm, v(-79.54, -40.4) * mm]});
            skFitSpline(sketch, "E268", {"points": [v(-79.54, -40.4) * mm, v(-79.45, -43.56) * mm, v(-79.4, -47.18) * mm, v(-79.4, -51.25) * mm]});
            skFitSpline(sketch, "E269", {"points": [v(-79.4, -51.25) * mm, v(-79.4, -53.1) * mm, v(-79.47, -54.91) * mm, v(-79.62, -56.71) * mm]});
            skFitSpline(sketch, "E270", {"points": [v(-79.62, -56.71) * mm, v(-79.71, -58.46) * mm, v(-79.76, -60.47) * mm, v(-79.76, -62.75) * mm]});
            skFitSpline(sketch, "E271", {"points": [v(-79.76, -62.75) * mm, v(-79.76, -69.88) * mm, v(-78.11, -75.1) * mm, v(-74.81, -78.4) * mm]});
            skFitSpline(sketch, "E272", {"points": [v(-74.81, -78.4) * mm, v(-71.51, -81.7) * mm, v(-66.22, -83.35) * mm, v(-58.95, -83.35) * mm]});
            skFitSpline(sketch, "E273", {"points": [v(-58.95, -83.35) * mm, v(-55.65, -83.35) * mm, v(-52.74, -82.89) * mm, v(-50.21, -81.96) * mm]});
            skFitSpline(sketch, "E274", {"points": [v(-50.21, -81.96) * mm, v(-47.64, -81.04) * mm, v(-45.48, -79.68) * mm, v(-43.74, -77.89) * mm]});
            skFitSpline(sketch, "E275", {"points": [v(-43.74, -77.89) * mm, v(-41.99, -76.1) * mm, v(-40.65, -73.91) * mm, v(-39.73, -71.34) * mm]});
            skFitSpline(sketch, "E276", {"points": [v(-39.73, -71.34) * mm, v(-38.76, -68.77) * mm, v(-38.25, -65.86) * mm, v(-38.2, -62.6) * mm]});
            skFitSpline(sketch, "E277", {"points": [v(-38.2, -62.6) * mm, v(-38.16, -59.94) * mm, v(-38.08, -57.2) * mm, v(-37.99, -54.38) * mm]});
            skFitSpline(sketch, "E278", {"points": [v(-37.99, -54.38) * mm, v(-37.89, -51.52) * mm, v(-37.8, -48.75) * mm, v(-37.7, -46.08) * mm]});
            skFitSpline(sketch, "E279", {"points": [v(-37.7, -46.08) * mm, v(-37.6, -43.37) * mm, v(-37.48, -40.84) * mm, v(-37.33, -38.51) * mm]});
            skFitSpline(sketch, "E280", {"points": [v(-37.33, -38.51) * mm, v(-37.18, -36.14) * mm, v(-37.04, -34.1) * mm, v(-36.9, -32.4) * mm]});
            skFitSpline(sketch, "E281", {"points": [v(-36.9, -32.4) * mm, v(-37.72, -32.64) * mm, v(-38.45, -32.77) * mm, v(-39.08, -32.77) * mm]});
            skFitSpline(sketch, "E282", {"points": [v(-39.08, -32.77) * mm, v(-39.56, -32.77) * mm, v(-40.05, -32.74) * mm, v(-40.53, -32.7) * mm]});
            skFitSpline(sketch, "E283", {"points": [v(-40.53, -32.7) * mm, v(-41.02, -32.6) * mm, v(-41.53, -32.5) * mm, v(-42.06, -32.4) * mm]});
            skFitSpline(sketch, "E284", {"points": [v(-42.06, -32.4) * mm, v(-41.87, -33.8) * mm, v(-41.75, -36.38) * mm, v(-41.7, -40.12) * mm]});
            skFitSpline(sketch, "E285", {"points": [v(-41.7, -40.12) * mm, v(-41.65, -43.85) * mm, v(-41.62, -49.17) * mm, v(-41.62, -56.06) * mm]});
            skFitSpline(sketch, "E286", {"points": [v(19.17, -83.35) * mm, v(19.17, -82.81) * mm, v(19.17, -82.01) * mm, v(19.17, -80.95) * mm]});
            skFitSpline(sketch, "E287", {"points": [v(19.17, -80.95) * mm, v(19.17, -79.78) * mm, v(19.14, -78.42) * mm, v(19.1, -76.87) * mm]});
            skFitSpline(sketch, "E288", {"points": [v(19.1, -76.87) * mm, v(19.1, -75.27) * mm, v(19.07, -73.57) * mm, v(19.02, -71.78) * mm]});
            skFitSpline(sketch, "E289", {"points": [v(19.02, -71.78) * mm, v(19.02, -69.93) * mm, v(19, -68.11) * mm, v(18.95, -66.32) * mm]});
            skFitSpline(sketch, "E290", {"points": [v(18.95, -66.32) * mm, v(18.95, -64.52) * mm, v(18.95, -62.8) * mm, v(18.95, -61.15) * mm]});
            skFitSpline(sketch, "E291", {"points": [v(18.95, -61.15) * mm, v(18.95, -59.45) * mm, v(18.95, -58) * mm, v(18.95, -56.78) * mm]});
            skFitSpline(sketch, "E292", {"points": [v(18.95, -56.78) * mm, v(18.95, -55.38) * mm, v(19, -53.5) * mm, v(19.1, -51.18) * mm]});
            skFitSpline(sketch, "E293", {"points": [v(19.1, -51.18) * mm, v(19.2, -48.85) * mm, v(19.29, -46.47) * mm, v(19.39, -44.05) * mm]});
            skFitSpline(sketch, "E294", {"points": [v(19.39, -44.05) * mm, v(19.53, -41.62) * mm, v(19.65, -39.34) * mm, v(19.75, -37.2) * mm]});
            skFitSpline(sketch, "E295", {"points": [v(19.75, -37.2) * mm, v(19.9, -35.07) * mm, v(20.02, -33.47) * mm, v(20.11, -32.4) * mm]});
            skFitSpline(sketch, "E296", {"points": [v(20.11, -32.4) * mm, v(19.14, -32.64) * mm, v(18.37, -32.77) * mm, v(17.79, -32.77) * mm]});
            skFitSpline(sketch, "E297", {"points": [v(17.79, -32.77) * mm, v(17.1, -32.77) * mm, v(16.28, -32.64) * mm, v(15.31, -32.4) * mm]});
            skFitSpline(sketch, "E298", {"points": [v(15.31, -32.4) * mm, v(15.55, -36.67) * mm, v(15.7, -41.23) * mm, v(15.75, -46.08) * mm]});
            skFitSpline(sketch, "E299", {"points": [v(15.75, -46.08) * mm, v(15.84, -50.89) * mm, v(15.9, -55.84) * mm, v(15.9, -60.93) * mm]});
            skLineSegment(sketch, "E300", {"start": v(18.15, -83.35) * mm, "end": v(19.17, -83.35) * mm});
            skLineSegment(sketch, "E301", {"start": v(19.17, -83.35) * mm, "end": v(18.15, -83.35) * mm});
            skFitSpline(sketch, "E302", {"points": [v(15.9, -70.83) * mm, v(13.66, -68.6) * mm, v(11.04, -65.9) * mm, v(8.03, -62.75) * mm]});
            skFitSpline(sketch, "E303", {"points": [v(8.03, -62.75) * mm, v(5.07, -59.55) * mm, v(1.92, -56.18) * mm, v(-1.43, -52.63) * mm]});
            skFitSpline(sketch, "E304", {"points": [v(-1.43, -52.63) * mm, v(-4.73, -49.04) * mm, v(-8.08, -45.43) * mm, v(-11.47, -41.8) * mm]});
            skFitSpline(sketch, "E305", {"points": [v(-11.47, -41.8) * mm, v(-14.82, -38.1) * mm, v(-17.97, -34.66) * mm, v(-20.93, -31.46) * mm]});
            skLineSegment(sketch, "E306", {"start": v(15.9, -60.93) * mm, "end": v(15.9, -70.83) * mm});
            skLineSegment(sketch, "E307", {"start": v(15.9, -70.83) * mm, "end": v(15.9, -60.93) * mm});
            skFitSpline(sketch, "E308", {"points": [v(-22.1, -31.46) * mm, v(-22, -33.1) * mm, v(-21.95, -35.6) * mm, v(-21.95, -38.95) * mm]});
            skFitSpline(sketch, "E309", {"points": [v(-21.95, -38.95) * mm, v(-21.9, -42.3) * mm, v(-21.88, -46.3) * mm, v(-21.88, -50.96) * mm]});
            skFitSpline(sketch, "E310", {"points": [v(-21.88, -50.96) * mm, v(-21.88, -52.56) * mm, v(-21.9, -54.38) * mm, v(-21.95, -56.42) * mm]});
            skFitSpline(sketch, "E311", {"points": [v(-21.95, -56.42) * mm, v(-22, -58.46) * mm, v(-22.07, -60.54) * mm, v(-22.17, -62.68) * mm]});
            skFitSpline(sketch, "E312", {"points": [v(-22.17, -62.68) * mm, v(-22.22, -64.81) * mm, v(-22.32, -66.95) * mm, v(-22.46, -69.08) * mm]});
            skFitSpline(sketch, "E313", {"points": [v(-22.46, -69.08) * mm, v(-22.56, -71.22) * mm, v(-22.66, -73.2) * mm, v(-22.75, -75.05) * mm]});
            skFitSpline(sketch, "E314", {"points": [v(-22.75, -75.05) * mm, v(-22.85, -76.85) * mm, v(-22.97, -78.4) * mm, v(-23.12, -79.7) * mm]});
            skFitSpline(sketch, "E315", {"points": [v(-23.12, -79.7) * mm, v(-23.21, -81.02) * mm, v(-23.31, -81.92) * mm, v(-23.4, -82.4) * mm]});
            skFitSpline(sketch, "E316", {"points": [v(-23.4, -82.4) * mm, v(-22.58, -82.3) * mm, v(-21.69, -82.26) * mm, v(-20.72, -82.26) * mm]});
            skFitSpline(sketch, "E317", {"points": [v(-20.72, -82.26) * mm, v(-19.8, -82.26) * mm, v(-18.94, -82.3) * mm, v(-18.17, -82.4) * mm]});
            skFitSpline(sketch, "E318", {"points": [v(-18.17, -82.4) * mm, v(-18.22, -82.01) * mm, v(-18.26, -81.29) * mm, v(-18.31, -80.22) * mm]});
            skFitSpline(sketch, "E319", {"points": [v(-18.31, -80.22) * mm, v(-18.36, -79.1) * mm, v(-18.41, -77.82) * mm, v(-18.46, -76.36) * mm]});
            skFitSpline(sketch, "E320", {"points": [v(-18.46, -76.36) * mm, v(-18.5, -74.9) * mm, v(-18.56, -73.33) * mm, v(-18.6, -71.63) * mm]});
            skFitSpline(sketch, "E321", {"points": [v(-18.6, -71.63) * mm, v(-18.65, -69.93) * mm, v(-18.7, -68.26) * mm, v(-18.75, -66.6) * mm]});
            skFitSpline(sketch, "E322", {"points": [v(-18.75, -66.6) * mm, v(-18.75, -64.96) * mm, v(-18.77, -63.38) * mm, v(-18.82, -61.88) * mm]});
            skFitSpline(sketch, "E323", {"points": [v(-18.82, -61.88) * mm, v(-18.82, -60.37) * mm, v(-18.82, -59.11) * mm, v(-18.82, -58.1) * mm]});
            skFitSpline(sketch, "E324", {"points": [v(-18.82, -58.1) * mm, v(-18.82, -54.16) * mm, v(-18.8, -51.06) * mm, v(-18.75, -48.78) * mm]});
            skFitSpline(sketch, "E325", {"points": [v(-18.75, -48.78) * mm, v(-18.7, -46.5) * mm, v(-18.65, -44.68) * mm, v(-18.6, -43.32) * mm]});
            skFitSpline(sketch, "E326", {"points": [v(-18.6, -43.32) * mm, v(-12.3, -50.01) * mm, v(-5.99, -56.76) * mm, v(0.32, -63.55) * mm]});
            skFitSpline(sketch, "E327", {"points": [v(0.32, -63.55) * mm, v(6.63, -70.3) * mm, v(12.57, -76.9) * mm, v(18.15, -83.35) * mm]});
            skLineSegment(sketch, "E328", {"start": v(-20.93, -31.46) * mm, "end": v(-22.1, -31.46) * mm});
            skLineSegment(sketch, "E329", {"start": v(-22.1, -31.46) * mm, "end": v(-20.93, -31.46) * mm});
            skFitSpline(sketch, "E330", {"points": [v(33.75, -63.77) * mm, v(33.75, -66.97) * mm, v(33.68, -70.13) * mm, v(33.53, -73.23) * mm]});
            skFitSpline(sketch, "E331", {"points": [v(33.53, -73.23) * mm, v(33.43, -76.34) * mm, v(33.31, -79.4) * mm, v(33.17, -82.4) * mm]});
            skFitSpline(sketch, "E332", {"points": [v(33.17, -82.4) * mm, v(34.82, -82.3) * mm, v(36.44, -82.26) * mm, v(38.04, -82.26) * mm]});
            skFitSpline(sketch, "E333", {"points": [v(38.04, -82.26) * mm, v(39.64, -82.26) * mm, v(41.27, -82.26) * mm, v(42.92, -82.26) * mm]});
            skFitSpline(sketch, "E334", {"points": [v(42.92, -82.26) * mm, v(44.57, -82.26) * mm, v(46.2, -82.28) * mm, v(47.8, -82.33) * mm]});
            skFitSpline(sketch, "E335", {"points": [v(47.8, -82.33) * mm, v(49.4, -82.38) * mm, v(51.02, -82.4) * mm, v(52.67, -82.4) * mm]});
            skFitSpline(sketch, "E336", {"points": [v(52.67, -82.4) * mm, v(55.54, -82.4) * mm, v(58.52, -81.99) * mm, v(61.62, -81.16) * mm]});
            skFitSpline(sketch, "E337", {"points": [v(61.62, -81.16) * mm, v(64.78, -80.3) * mm, v(67.64, -78.84) * mm, v(70.21, -76.8) * mm]});
            skFitSpline(sketch, "E338", {"points": [v(70.21, -76.8) * mm, v(72.83, -74.76) * mm, v(74.97, -72.1) * mm, v(76.62, -68.8) * mm]});
            skFitSpline(sketch, "E339", {"points": [v(76.62, -68.8) * mm, v(78.32, -65.44) * mm, v(79.16, -61.34) * mm, v(79.16, -56.5) * mm]});
            skFitSpline(sketch, "E340", {"points": [v(79.16, -56.5) * mm, v(79.16, -52.76) * mm, v(78.7, -49.4) * mm, v(77.78, -46.45) * mm]});
            skFitSpline(sketch, "E341", {"points": [v(77.78, -46.45) * mm, v(76.9, -43.44) * mm, v(75.5, -40.92) * mm, v(73.56, -38.88) * mm]});
            skFitSpline(sketch, "E342", {"points": [v(73.56, -38.88) * mm, v(71.62, -36.8) * mm, v(69.12, -35.2) * mm, v(66.06, -34.08) * mm]});
            skFitSpline(sketch, "E343", {"points": [v(66.06, -34.08) * mm, v(63.06, -32.96) * mm, v(59.42, -32.4) * mm, v(55.15, -32.4) * mm]});
            skFitSpline(sketch, "E344", {"points": [v(55.15, -32.4) * mm, v(53.3, -32.4) * mm, v(51.46, -32.47) * mm, v(49.62, -32.62) * mm]});
            skFitSpline(sketch, "E345", {"points": [v(49.62, -32.62) * mm, v(47.82, -32.72) * mm, v(46, -32.77) * mm, v(44.16, -32.77) * mm]});
            skFitSpline(sketch, "E346", {"points": [v(44.16, -32.77) * mm, v(42.31, -32.77) * mm, v(40.47, -32.74) * mm, v(38.63, -32.7) * mm]});
            skFitSpline(sketch, "E347", {"points": [v(38.63, -32.7) * mm, v(36.83, -32.6) * mm, v(35.01, -32.5) * mm, v(33.17, -32.4) * mm]});
            skFitSpline(sketch, "E348", {"points": [v(33.17, -32.4) * mm, v(33.31, -35.6) * mm, v(33.43, -38.76) * mm, v(33.53, -41.86) * mm]});
            skFitSpline(sketch, "E349", {"points": [v(33.53, -41.86) * mm, v(33.68, -44.92) * mm, v(33.75, -48.05) * mm, v(33.75, -51.25) * mm]});
            skLineSegment(sketch, "E350", {"start": v(33.75, -51.25) * mm, "end": v(33.75, -63.77) * mm});
            skLineSegment(sketch, "E351", {"start": v(33.75, -63.77) * mm, "end": v(33.75, -51.25) * mm});
            skFitSpline(sketch, "E352", {"points": [v(39.72, -51.25) * mm, v(39.72, -48.63) * mm, v(39.74, -46.06) * mm, v(39.8, -43.54) * mm]});
            skFitSpline(sketch, "E353", {"points": [v(39.8, -43.54) * mm, v(39.89, -40.97) * mm, v(40, -38.51) * mm, v(40.15, -36.19) * mm]});
            skFitSpline(sketch, "E354", {"points": [v(40.15, -36.19) * mm, v(41.66, -36) * mm, v(43.36, -35.82) * mm, v(45.25, -35.68) * mm]});
            skFitSpline(sketch, "E355", {"points": [v(45.25, -35.68) * mm, v(47.14, -35.53) * mm, v(49.18, -35.46) * mm, v(51.36, -35.46) * mm]});
            skFitSpline(sketch, "E356", {"points": [v(51.36, -35.46) * mm, v(54.37, -35.46) * mm, v(57.14, -35.77) * mm, v(59.66, -36.4) * mm]});
            skFitSpline(sketch, "E357", {"points": [v(59.66, -36.4) * mm, v(62.18, -36.99) * mm, v(64.34, -38.08) * mm, v(66.14, -39.68) * mm]});
            skFitSpline(sketch, "E358", {"points": [v(66.14, -39.68) * mm, v(67.98, -41.23) * mm, v(69.41, -43.37) * mm, v(70.43, -46.08) * mm]});
            skFitSpline(sketch, "E359", {"points": [v(70.43, -46.08) * mm, v(71.5, -48.8) * mm, v(72.03, -52.27) * mm, v(72.03, -56.5) * mm]});
            skFitSpline(sketch, "E360", {"points": [v(72.03, -56.5) * mm, v(72.03, -61.3) * mm, v(71.35, -65.23) * mm, v(70, -68.28) * mm]});
            skFitSpline(sketch, "E361", {"points": [v(70, -68.28) * mm, v(68.68, -71.3) * mm, v(66.96, -73.67) * mm, v(64.83, -75.41) * mm]});
            skFitSpline(sketch, "E362", {"points": [v(64.83, -75.41) * mm, v(62.74, -77.16) * mm, v(60.36, -78.35) * mm, v(57.7, -78.98) * mm]});
            skFitSpline(sketch, "E363", {"points": [v(57.7, -78.98) * mm, v(55.03, -79.61) * mm, v(52.36, -79.93) * mm, v(49.69, -79.93) * mm]});
            skFitSpline(sketch, "E364", {"points": [v(49.69, -79.93) * mm, v(47.84, -79.93) * mm, v(46.05, -79.88) * mm, v(44.3, -79.78) * mm]});
            skFitSpline(sketch, "E365", {"points": [v(44.3, -79.78) * mm, v(42.56, -79.64) * mm, v(41.17, -79.44) * mm, v(40.15, -79.2) * mm]});
            skFitSpline(sketch, "E366", {"points": [v(40.15, -79.2) * mm, v(39.86, -74.15) * mm, v(39.72, -69) * mm, v(39.72, -63.77) * mm]});
            skLineSegment(sketch, "E367", {"start": v(39.72, -63.77) * mm, "end": v(39.72, -51.25) * mm});
            skLineSegment(sketch, "E368", {"start": v(39.72, -51.25) * mm, "end": v(39.72, -63.77) * mm});
            skSolve(sketch);
        }
        {
            var Q0;
            Q0=makeQuery(id+"F0.imprint","IMPRINT",FACE,{"disambiguationData":[TD([[makeQuery(id+"F0.imprint","IMPRINT",EDGE,{"derivedFrom":sQuery(id+"F0.wireOp",EDGE,"E0")}),1.0]])]});
            var Q1;
            Q1=makeQuery(id+"F0.imprint","IMPRINT",FACE,{"disambiguationData":[TD([[makeQuery(id+"F0.imprint","IMPRINT",EDGE,{"derivedFrom":sQuery(id+"F0.wireOp",EDGE,"E48")}),1.0]])]});
            var Q2;
            Q2=makeQuery(id+"F0.imprint","IMPRINT",FACE,{"disambiguationData":[TD([[makeQuery(id+"F0.imprint","IMPRINT",EDGE,{"derivedFrom":sQuery(id+"F0.wireOp",EDGE,"E76")}),1.0]])]});
            var Q3;
            Q3=makeQuery(id+"F0.imprint","IMPRINT",FACE,{"disambiguationData":[TD([[makeQuery(id+"F0.imprint","IMPRINT",EDGE,{"derivedFrom":sQuery(id+"F0.wireOp",EDGE,"E94")}),1.0]])]});
            var Q4;
            Q4=makeQuery(id+"F0.imprint","IMPRINT",FACE,{"disambiguationData":[TD([[makeQuery(id+"F0.imprint","IMPRINT",EDGE,{"derivedFrom":sQuery(id+"F0.wireOp",EDGE,"E138")}),-1.0]])]});
            var Q5;
            Q5=makeQuery(id+"F0.imprint","IMPRINT",FACE,{"disambiguationData":[TD([[makeQuery(id+"F0.imprint","IMPRINT",EDGE,{"derivedFrom":sQuery(id+"F0.wireOp",EDGE,"E171")}),1.0]])]});
            var Q6;
            Q6=makeQuery(id+"F0.imprint","IMPRINT",FACE,{"disambiguationData":[TD([[makeQuery(id+"F0.imprint","IMPRINT",EDGE,{"derivedFrom":sQuery(id+"F0.wireOp",EDGE,"E219")}),1.0]])]});
            var Q7;
            Q7=makeQuery(id+"F0.imprint","IMPRINT",FACE,{"disambiguationData":[TD([[makeQuery(id+"F0.imprint","IMPRINT",EDGE,{"derivedFrom":sQuery(id+"F0.wireOp",EDGE,"E247")}),1.0]])]});
            var Q8;
            Q8=makeQuery(id+"F0.imprint","IMPRINT",FACE,{"disambiguationData":[TD([[makeQuery(id+"F0.imprint","IMPRINT",EDGE,{"derivedFrom":sQuery(id+"F0.wireOp",EDGE,"E116")}),1.0]])]});
            var Q9;
            Q9=makeQuery(id+"F0.imprint","IMPRINT",FACE,{"disambiguationData":[TD([[makeQuery(id+"F0.imprint","IMPRINT",EDGE,{"derivedFrom":sQuery(id+"F0.wireOp",EDGE,"E286")}),1.0]])]});
            var Q10;
            Q10=makeQuery(id+"F0.imprint","IMPRINT",FACE,{"disambiguationData":[TD([[makeQuery(id+"F0.imprint","IMPRINT",EDGE,{"derivedFrom":sQuery(id+"F0.wireOp",EDGE,"E330")}),1.0]])]});
            extrude(context, id + "F1", {"entities" : qUnion([Q0, Q1, Q2, Q3, Q4, Q5, Q6, Q7, Q8, Q9, Q10]), "depth" : 2 * mm});
        }
        {
            var Q0;
            Q0=makeQuery(id+"F1.opExtrude","CAP_EDGE",EDGE,{"disambiguationData":[OSD([sQuery(id+"F0.wireOp",EDGE,"E12")])],"isStart":false});
            var Q1;
            Q1=makeQuery(id+"F1.opExtrude","CAP_EDGE",EDGE,{"disambiguationData":[OSD([sQuery(id+"F0.wireOp",EDGE,"E8")])],"isStart":false});
            var Q2;
            Q2=makeQuery(id+"F1.opExtrude","CAP_EDGE",EDGE,{"disambiguationData":[OSD([sQuery(id+"F0.wireOp",EDGE,"E10")])],"isStart":false});
            var Q3;
            Q3=makeQuery(id+"F1.opExtrude","CAP_FACE",FACE,{"disambiguationData":[OSD([sQuery(id+"F0.wireOp",EDGE,"E0"),sQuery(id+"F0.wireOp",EDGE,"E1"),sQuery(id+"F0.wireOp",EDGE,"E2"),sQuery(id+"F0.wireOp",EDGE,"E3"),sQuery(id+"F0.wireOp",EDGE,"E4"),sQuery(id+"F0.wireOp",EDGE,"E5"),sQuery(id+"F0.wireOp",EDGE,"E6"),sQuery(id+"F0.wireOp",EDGE,"E7"),sQuery(id+"F0.wireOp",EDGE,"E8"),sQuery(id+"F0.wireOp",EDGE,"E9"),sQuery(id+"F0.wireOp",EDGE,"E10"),sQuery(id+"F0.wireOp",EDGE,"E11"),sQuery(id+"F0.wireOp",EDGE,"E12"),sQuery(id+"F0.wireOp",EDGE,"E13"),sQuery(id+"F0.wireOp",EDGE,"E14"),sQuery(id+"F0.wireOp",EDGE,"E15"),sQuery(id+"F0.wireOp",EDGE,"E16"),sQuery(id+"F0.wireOp",EDGE,"E17"),sQuery(id+"F0.wireOp",EDGE,"E18"),sQuery(id+"F0.wireOp",EDGE,"E19"),sQuery(id+"F0.wireOp",EDGE,"E20"),sQuery(id+"F0.wireOp",EDGE,"E21"),sQuery(id+"F0.wireOp",EDGE,"E23"),sQuery(id+"F0.wireOp",EDGE,"E24"),sQuery(id+"F0.wireOp",EDGE,"E25"),sQuery(id+"F0.wireOp",EDGE,"E26"),sQuery(id+"F0.wireOp",EDGE,"E27"),sQuery(id+"F0.wireOp",EDGE,"E28"),sQuery(id+"F0.wireOp",EDGE,"E29"),sQuery(id+"F0.wireOp",EDGE,"E30"),sQuery(id+"F0.wireOp",EDGE,"E31"),sQuery(id+"F0.wireOp",EDGE,"E32"),sQuery(id+"F0.wireOp",EDGE,"E33"),sQuery(id+"F0.wireOp",EDGE,"E34"),sQuery(id+"F0.wireOp",EDGE,"E35"),sQuery(id+"F0.wireOp",EDGE,"E36"),sQuery(id+"F0.wireOp",EDGE,"E37"),sQuery(id+"F0.wireOp",EDGE,"E38"),sQuery(id+"F0.wireOp",EDGE,"E39"),sQuery(id+"F0.wireOp",EDGE,"E40"),sQuery(id+"F0.wireOp",EDGE,"E41"),sQuery(id+"F0.wireOp",EDGE,"E42"),sQuery(id+"F0.wireOp",EDGE,"E43"),sQuery(id+"F0.wireOp",EDGE,"E44"),sQuery(id+"F0.wireOp",EDGE,"E45"),sQuery(id+"F0.wireOp",EDGE,"E47")])],"isStart":false});
            var Q4;
            Q4=makeQuery(id+"F1.opExtrude","CAP_FACE",FACE,{"disambiguationData":[OSD([sQuery(id+"F0.wireOp",EDGE,"E48"),sQuery(id+"F0.wireOp",EDGE,"E49"),sQuery(id+"F0.wireOp",EDGE,"E50"),sQuery(id+"F0.wireOp",EDGE,"E51"),sQuery(id+"F0.wireOp",EDGE,"E52"),sQuery(id+"F0.wireOp",EDGE,"E53"),sQuery(id+"F0.wireOp",EDGE,"E55"),sQuery(id+"F0.wireOp",EDGE,"E56"),sQuery(id+"F0.wireOp",EDGE,"E57"),sQuery(id+"F0.wireOp",EDGE,"E58"),sQuery(id+"F0.wireOp",EDGE,"E59"),sQuery(id+"F0.wireOp",EDGE,"E60"),sQuery(id+"F0.wireOp",EDGE,"E61"),sQuery(id+"F0.wireOp",EDGE,"E62"),sQuery(id+"F0.wireOp",EDGE,"E63"),sQuery(id+"F0.wireOp",EDGE,"E64"),sQuery(id+"F0.wireOp",EDGE,"E65"),sQuery(id+"F0.wireOp",EDGE,"E66"),sQuery(id+"F0.wireOp",EDGE,"E67"),sQuery(id+"F0.wireOp",EDGE,"E68"),sQuery(id+"F0.wireOp",EDGE,"E69"),sQuery(id+"F0.wireOp",EDGE,"E70"),sQuery(id+"F0.wireOp",EDGE,"E71"),sQuery(id+"F0.wireOp",EDGE,"E72"),sQuery(id+"F0.wireOp",EDGE,"E73"),sQuery(id+"F0.wireOp",EDGE,"E75")])],"isStart":false});
            var Q5;
            Q5=makeQuery(id+"F1.opExtrude","CAP_FACE",FACE,{"disambiguationData":[OSD([sQuery(id+"F0.wireOp",EDGE,"E76"),sQuery(id+"F0.wireOp",EDGE,"E77"),sQuery(id+"F0.wireOp",EDGE,"E78"),sQuery(id+"F0.wireOp",EDGE,"E79"),sQuery(id+"F0.wireOp",EDGE,"E80"),sQuery(id+"F0.wireOp",EDGE,"E81"),sQuery(id+"F0.wireOp",EDGE,"E83"),sQuery(id+"F0.wireOp",EDGE,"E84"),sQuery(id+"F0.wireOp",EDGE,"E85"),sQuery(id+"F0.wireOp",EDGE,"E86"),sQuery(id+"F0.wireOp",EDGE,"E87"),sQuery(id+"F0.wireOp",EDGE,"E88"),sQuery(id+"F0.wireOp",EDGE,"E89"),sQuery(id+"F0.wireOp",EDGE,"E90"),sQuery(id+"F0.wireOp",EDGE,"E91"),sQuery(id+"F0.wireOp",EDGE,"E93")])],"isStart":false});
            var Q6;
            Q6=makeQuery(id+"F1.opExtrude","CAP_FACE",FACE,{"disambiguationData":[OSD([sQuery(id+"F0.wireOp",EDGE,"E94"),sQuery(id+"F0.wireOp",EDGE,"E95"),sQuery(id+"F0.wireOp",EDGE,"E96"),sQuery(id+"F0.wireOp",EDGE,"E97"),sQuery(id+"F0.wireOp",EDGE,"E98"),sQuery(id+"F0.wireOp",EDGE,"E99"),sQuery(id+"F0.wireOp",EDGE,"E100"),sQuery(id+"F0.wireOp",EDGE,"E101"),sQuery(id+"F0.wireOp",EDGE,"E102"),sQuery(id+"F0.wireOp",EDGE,"E103"),sQuery(id+"F0.wireOp",EDGE,"E104"),sQuery(id+"F0.wireOp",EDGE,"E105"),sQuery(id+"F0.wireOp",EDGE,"E106"),sQuery(id+"F0.wireOp",EDGE,"E107"),sQuery(id+"F0.wireOp",EDGE,"E108"),sQuery(id+"F0.wireOp",EDGE,"E109"),sQuery(id+"F0.wireOp",EDGE,"E110"),sQuery(id+"F0.wireOp",EDGE,"E111"),sQuery(id+"F0.wireOp",EDGE,"E112"),sQuery(id+"F0.wireOp",EDGE,"E113"),sQuery(id+"F0.wireOp",EDGE,"E115")])],"isStart":false});
            var Q7;
            Q7=makeQuery(id+"F1.opExtrude","CAP_FACE",FACE,{"disambiguationData":[OSD([sQuery(id+"F0.wireOp",EDGE,"E116"),sQuery(id+"F0.wireOp",EDGE,"E117"),sQuery(id+"F0.wireOp",EDGE,"E118"),sQuery(id+"F0.wireOp",EDGE,"E119"),sQuery(id+"F0.wireOp",EDGE,"E120"),sQuery(id+"F0.wireOp",EDGE,"E121"),sQuery(id+"F0.wireOp",EDGE,"E122"),sQuery(id+"F0.wireOp",EDGE,"E123"),sQuery(id+"F0.wireOp",EDGE,"E124"),sQuery(id+"F0.wireOp",EDGE,"E125"),sQuery(id+"F0.wireOp",EDGE,"E126"),sQuery(id+"F0.wireOp",EDGE,"E127"),sQuery(id+"F0.wireOp",EDGE,"E128"),sQuery(id+"F0.wireOp",EDGE,"E129"),sQuery(id+"F0.wireOp",EDGE,"E130"),sQuery(id+"F0.wireOp",EDGE,"E131"),sQuery(id+"F0.wireOp",EDGE,"E132"),sQuery(id+"F0.wireOp",EDGE,"E133"),sQuery(id+"F0.wireOp",EDGE,"E134"),sQuery(id+"F0.wireOp",EDGE,"E135"),sQuery(id+"F0.wireOp",EDGE,"E137")])],"isStart":false});
            var Q8;
            Q8=makeQuery(id+"F1.opExtrude","CAP_FACE",FACE,{"disambiguationData":[OSD([sQuery(id+"F0.wireOp",EDGE,"E138"),sQuery(id+"F0.wireOp",EDGE,"E139"),sQuery(id+"F0.wireOp",EDGE,"E140"),sQuery(id+"F0.wireOp",EDGE,"E141"),sQuery(id+"F0.wireOp",EDGE,"E142"),sQuery(id+"F0.wireOp",EDGE,"E143"),sQuery(id+"F0.wireOp",EDGE,"E144"),sQuery(id+"F0.wireOp",EDGE,"E145"),sQuery(id+"F0.wireOp",EDGE,"E146"),sQuery(id+"F0.wireOp",EDGE,"E147"),sQuery(id+"F0.wireOp",EDGE,"E148"),sQuery(id+"F0.wireOp",EDGE,"E149"),sQuery(id+"F0.wireOp",EDGE,"E150"),sQuery(id+"F0.wireOp",EDGE,"E151"),sQuery(id+"F0.wireOp",EDGE,"E152"),sQuery(id+"F0.wireOp",EDGE,"E153"),sQuery(id+"F0.wireOp",EDGE,"E154"),sQuery(id+"F0.wireOp",EDGE,"E155"),sQuery(id+"F0.wireOp",EDGE,"E156"),sQuery(id+"F0.wireOp",EDGE,"E157"),sQuery(id+"F0.wireOp",EDGE,"E158"),sQuery(id+"F0.wireOp",EDGE,"E159"),sQuery(id+"F0.wireOp",EDGE,"E160"),sQuery(id+"F0.wireOp",EDGE,"E161"),sQuery(id+"F0.wireOp",EDGE,"E163"),sQuery(id+"F0.wireOp",EDGE,"E164"),sQuery(id+"F0.wireOp",EDGE,"E165"),sQuery(id+"F0.wireOp",EDGE,"E166"),sQuery(id+"F0.wireOp",EDGE,"E167"),sQuery(id+"F0.wireOp",EDGE,"E168"),sQuery(id+"F0.wireOp",EDGE,"E170")])],"isStart":false});
            var Q9;
            Q9=makeQuery(id+"F1.opExtrude","CAP_FACE",FACE,{"disambiguationData":[OSD([sQuery(id+"F0.wireOp",EDGE,"E171"),sQuery(id+"F0.wireOp",EDGE,"E172"),sQuery(id+"F0.wireOp",EDGE,"E173"),sQuery(id+"F0.wireOp",EDGE,"E174"),sQuery(id+"F0.wireOp",EDGE,"E175"),sQuery(id+"F0.wireOp",EDGE,"E176"),sQuery(id+"F0.wireOp",EDGE,"E177"),sQuery(id+"F0.wireOp",EDGE,"E178"),sQuery(id+"F0.wireOp",EDGE,"E179"),sQuery(id+"F0.wireOp",EDGE,"E180"),sQuery(id+"F0.wireOp",EDGE,"E181"),sQuery(id+"F0.wireOp",EDGE,"E182"),sQuery(id+"F0.wireOp",EDGE,"E183"),sQuery(id+"F0.wireOp",EDGE,"E184"),sQuery(id+"F0.wireOp",EDGE,"E185"),sQuery(id+"F0.wireOp",EDGE,"E186"),sQuery(id+"F0.wireOp",EDGE,"E187"),sQuery(id+"F0.wireOp",EDGE,"E188"),sQuery(id+"F0.wireOp",EDGE,"E189"),sQuery(id+"F0.wireOp",EDGE,"E190"),sQuery(id+"F0.wireOp",EDGE,"E191"),sQuery(id+"F0.wireOp",EDGE,"E192"),sQuery(id+"F0.wireOp",EDGE,"E194"),sQuery(id+"F0.wireOp",EDGE,"E195"),sQuery(id+"F0.wireOp",EDGE,"E196"),sQuery(id+"F0.wireOp",EDGE,"E197"),sQuery(id+"F0.wireOp",EDGE,"E198"),sQuery(id+"F0.wireOp",EDGE,"E199"),sQuery(id+"F0.wireOp",EDGE,"E200"),sQuery(id+"F0.wireOp",EDGE,"E201"),sQuery(id+"F0.wireOp",EDGE,"E202"),sQuery(id+"F0.wireOp",EDGE,"E203"),sQuery(id+"F0.wireOp",EDGE,"E204"),sQuery(id+"F0.wireOp",EDGE,"E205"),sQuery(id+"F0.wireOp",EDGE,"E206"),sQuery(id+"F0.wireOp",EDGE,"E207"),sQuery(id+"F0.wireOp",EDGE,"E208"),sQuery(id+"F0.wireOp",EDGE,"E209"),sQuery(id+"F0.wireOp",EDGE,"E210"),sQuery(id+"F0.wireOp",EDGE,"E211"),sQuery(id+"F0.wireOp",EDGE,"E212"),sQuery(id+"F0.wireOp",EDGE,"E213"),sQuery(id+"F0.wireOp",EDGE,"E214"),sQuery(id+"F0.wireOp",EDGE,"E215"),sQuery(id+"F0.wireOp",EDGE,"E216"),sQuery(id+"F0.wireOp",EDGE,"E218")])],"isStart":false});
            var Q10;
            Q10=makeQuery(id+"F1.opExtrude","CAP_FACE",FACE,{"disambiguationData":[OSD([sQuery(id+"F0.wireOp",EDGE,"E219"),sQuery(id+"F0.wireOp",EDGE,"E220"),sQuery(id+"F0.wireOp",EDGE,"E221"),sQuery(id+"F0.wireOp",EDGE,"E222"),sQuery(id+"F0.wireOp",EDGE,"E223"),sQuery(id+"F0.wireOp",EDGE,"E224"),sQuery(id+"F0.wireOp",EDGE,"E226"),sQuery(id+"F0.wireOp",EDGE,"E227"),sQuery(id+"F0.wireOp",EDGE,"E228"),sQuery(id+"F0.wireOp",EDGE,"E229"),sQuery(id+"F0.wireOp",EDGE,"E230"),sQuery(id+"F0.wireOp",EDGE,"E231"),sQuery(id+"F0.wireOp",EDGE,"E232"),sQuery(id+"F0.wireOp",EDGE,"E233"),sQuery(id+"F0.wireOp",EDGE,"E234"),sQuery(id+"F0.wireOp",EDGE,"E235"),sQuery(id+"F0.wireOp",EDGE,"E236"),sQuery(id+"F0.wireOp",EDGE,"E237"),sQuery(id+"F0.wireOp",EDGE,"E238"),sQuery(id+"F0.wireOp",EDGE,"E239"),sQuery(id+"F0.wireOp",EDGE,"E240"),sQuery(id+"F0.wireOp",EDGE,"E241"),sQuery(id+"F0.wireOp",EDGE,"E242"),sQuery(id+"F0.wireOp",EDGE,"E243"),sQuery(id+"F0.wireOp",EDGE,"E244"),sQuery(id+"F0.wireOp",EDGE,"E246")])],"isStart":false});
            var Q11;
            Q11=makeQuery(id+"F1.opExtrude","CAP_FACE",FACE,{"disambiguationData":[OSD([sQuery(id+"F0.wireOp",EDGE,"E247"),sQuery(id+"F0.wireOp",EDGE,"E248"),sQuery(id+"F0.wireOp",EDGE,"E249"),sQuery(id+"F0.wireOp",EDGE,"E250"),sQuery(id+"F0.wireOp",EDGE,"E251"),sQuery(id+"F0.wireOp",EDGE,"E252"),sQuery(id+"F0.wireOp",EDGE,"E253"),sQuery(id+"F0.wireOp",EDGE,"E254"),sQuery(id+"F0.wireOp",EDGE,"E255"),sQuery(id+"F0.wireOp",EDGE,"E256"),sQuery(id+"F0.wireOp",EDGE,"E257"),sQuery(id+"F0.wireOp",EDGE,"E258"),sQuery(id+"F0.wireOp",EDGE,"E259"),sQuery(id+"F0.wireOp",EDGE,"E260"),sQuery(id+"F0.wireOp",EDGE,"E261"),sQuery(id+"F0.wireOp",EDGE,"E262"),sQuery(id+"F0.wireOp",EDGE,"E263"),sQuery(id+"F0.wireOp",EDGE,"E264"),sQuery(id+"F0.wireOp",EDGE,"E265"),sQuery(id+"F0.wireOp",EDGE,"E266"),sQuery(id+"F0.wireOp",EDGE,"E267"),sQuery(id+"F0.wireOp",EDGE,"E268"),sQuery(id+"F0.wireOp",EDGE,"E269"),sQuery(id+"F0.wireOp",EDGE,"E270"),sQuery(id+"F0.wireOp",EDGE,"E271"),sQuery(id+"F0.wireOp",EDGE,"E272"),sQuery(id+"F0.wireOp",EDGE,"E273"),sQuery(id+"F0.wireOp",EDGE,"E274"),sQuery(id+"F0.wireOp",EDGE,"E275"),sQuery(id+"F0.wireOp",EDGE,"E276"),sQuery(id+"F0.wireOp",EDGE,"E277"),sQuery(id+"F0.wireOp",EDGE,"E278"),sQuery(id+"F0.wireOp",EDGE,"E279"),sQuery(id+"F0.wireOp",EDGE,"E280"),sQuery(id+"F0.wireOp",EDGE,"E281"),sQuery(id+"F0.wireOp",EDGE,"E282"),sQuery(id+"F0.wireOp",EDGE,"E283"),sQuery(id+"F0.wireOp",EDGE,"E284"),sQuery(id+"F0.wireOp",EDGE,"E285")])],"isStart":false});
            var Q12;
            Q12=makeQuery(id+"F1.opExtrude","CAP_FACE",FACE,{"disambiguationData":[OSD([sQuery(id+"F0.wireOp",EDGE,"E286"),sQuery(id+"F0.wireOp",EDGE,"E287"),sQuery(id+"F0.wireOp",EDGE,"E288"),sQuery(id+"F0.wireOp",EDGE,"E289"),sQuery(id+"F0.wireOp",EDGE,"E290"),sQuery(id+"F0.wireOp",EDGE,"E291"),sQuery(id+"F0.wireOp",EDGE,"E292"),sQuery(id+"F0.wireOp",EDGE,"E293"),sQuery(id+"F0.wireOp",EDGE,"E294"),sQuery(id+"F0.wireOp",EDGE,"E295"),sQuery(id+"F0.wireOp",EDGE,"E296"),sQuery(id+"F0.wireOp",EDGE,"E297"),sQuery(id+"F0.wireOp",EDGE,"E298"),sQuery(id+"F0.wireOp",EDGE,"E299"),sQuery(id+"F0.wireOp",EDGE,"E301"),sQuery(id+"F0.wireOp",EDGE,"E302"),sQuery(id+"F0.wireOp",EDGE,"E303"),sQuery(id+"F0.wireOp",EDGE,"E304"),sQuery(id+"F0.wireOp",EDGE,"E305"),sQuery(id+"F0.wireOp",EDGE,"E307"),sQuery(id+"F0.wireOp",EDGE,"E308"),sQuery(id+"F0.wireOp",EDGE,"E309"),sQuery(id+"F0.wireOp",EDGE,"E310"),sQuery(id+"F0.wireOp",EDGE,"E311"),sQuery(id+"F0.wireOp",EDGE,"E312"),sQuery(id+"F0.wireOp",EDGE,"E313"),sQuery(id+"F0.wireOp",EDGE,"E314"),sQuery(id+"F0.wireOp",EDGE,"E315"),sQuery(id+"F0.wireOp",EDGE,"E316"),sQuery(id+"F0.wireOp",EDGE,"E317"),sQuery(id+"F0.wireOp",EDGE,"E318"),sQuery(id+"F0.wireOp",EDGE,"E319"),sQuery(id+"F0.wireOp",EDGE,"E320"),sQuery(id+"F0.wireOp",EDGE,"E321"),sQuery(id+"F0.wireOp",EDGE,"E322"),sQuery(id+"F0.wireOp",EDGE,"E323"),sQuery(id+"F0.wireOp",EDGE,"E324"),sQuery(id+"F0.wireOp",EDGE,"E325"),sQuery(id+"F0.wireOp",EDGE,"E326"),sQuery(id+"F0.wireOp",EDGE,"E327"),sQuery(id+"F0.wireOp",EDGE,"E329")])],"isStart":false});
            var Q13;
            Q13=makeQuery(id+"F1.opExtrude","CAP_FACE",FACE,{"disambiguationData":[OSD([sQuery(id+"F0.wireOp",EDGE,"E330"),sQuery(id+"F0.wireOp",EDGE,"E331"),sQuery(id+"F0.wireOp",EDGE,"E332"),sQuery(id+"F0.wireOp",EDGE,"E333"),sQuery(id+"F0.wireOp",EDGE,"E334"),sQuery(id+"F0.wireOp",EDGE,"E335"),sQuery(id+"F0.wireOp",EDGE,"E336"),sQuery(id+"F0.wireOp",EDGE,"E337"),sQuery(id+"F0.wireOp",EDGE,"E338"),sQuery(id+"F0.wireOp",EDGE,"E339"),sQuery(id+"F0.wireOp",EDGE,"E340"),sQuery(id+"F0.wireOp",EDGE,"E341"),sQuery(id+"F0.wireOp",EDGE,"E342"),sQuery(id+"F0.wireOp",EDGE,"E343"),sQuery(id+"F0.wireOp",EDGE,"E344"),sQuery(id+"F0.wireOp",EDGE,"E345"),sQuery(id+"F0.wireOp",EDGE,"E346"),sQuery(id+"F0.wireOp",EDGE,"E347"),sQuery(id+"F0.wireOp",EDGE,"E348"),sQuery(id+"F0.wireOp",EDGE,"E349"),sQuery(id+"F0.wireOp",EDGE,"E351"),sQuery(id+"F0.wireOp",EDGE,"E352"),sQuery(id+"F0.wireOp",EDGE,"E353"),sQuery(id+"F0.wireOp",EDGE,"E354"),sQuery(id+"F0.wireOp",EDGE,"E355"),sQuery(id+"F0.wireOp",EDGE,"E356"),sQuery(id+"F0.wireOp",EDGE,"E357"),sQuery(id+"F0.wireOp",EDGE,"E358"),sQuery(id+"F0.wireOp",EDGE,"E359"),sQuery(id+"F0.wireOp",EDGE,"E360"),sQuery(id+"F0.wireOp",EDGE,"E361"),sQuery(id+"F0.wireOp",EDGE,"E362"),sQuery(id+"F0.wireOp",EDGE,"E363"),sQuery(id+"F0.wireOp",EDGE,"E364"),sQuery(id+"F0.wireOp",EDGE,"E365"),sQuery(id+"F0.wireOp",EDGE,"E366"),sQuery(id+"F0.wireOp",EDGE,"E368")])],"isStart":false});
            fillet(context, id + "F2", {"entities" : qUnion([Q0, Q1, Q2, Q3, Q4, Q5, Q6, Q7, Q8, Q9, Q10, Q11, Q12, Q13]), "radius" : 1 * mm, "tangentPropagation" : true, "allowEdgeOverflow" : false});
        }
    });
